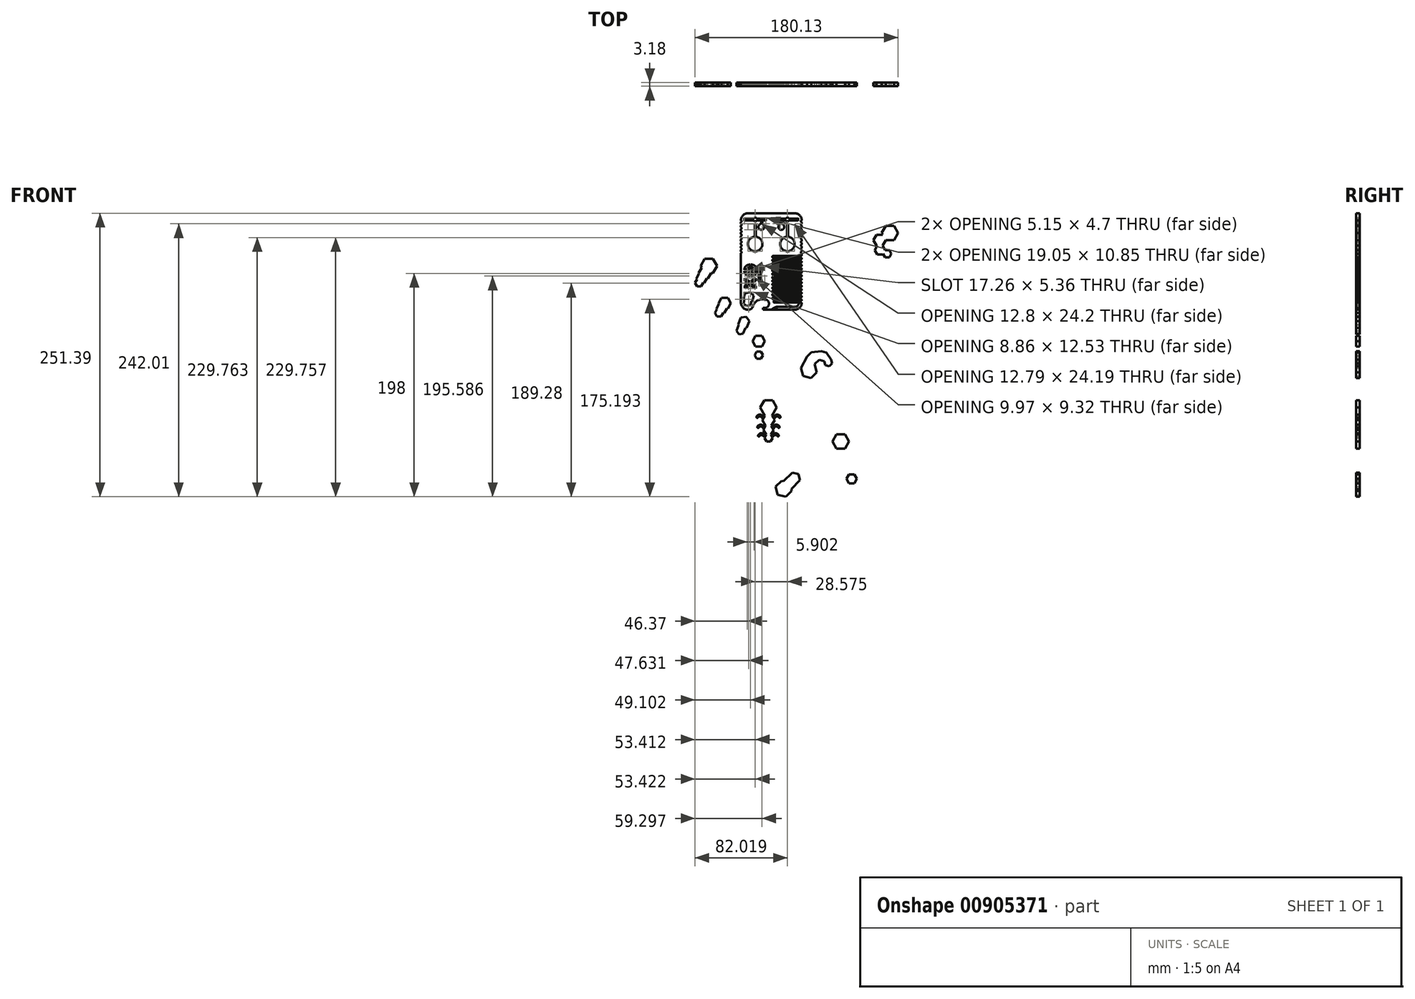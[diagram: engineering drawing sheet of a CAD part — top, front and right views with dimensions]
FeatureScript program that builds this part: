
annotation { "Feature Type Name" : "Feature", "Feature Type Description" : "" }
export const myFeature = defineFeature(function(context is Context, id is Id, definition is map)
    precondition{}
    {
        {
            var Q0;
            Q0=qCreatedBy(makeId("Front.planeOp"),FACE);
            var sketch = newSketch(context, id + "F0", { "sketchPlane" : qUnion([Q0])});
            skLineSegment(sketch, "E0.bottom", {"start": v(-20.64, 42.8) * mm, "end": v(20.64, 42.8) * mm});
            skLineSegment(sketch, "E0.top", {"start": v(-20.64, -42.8) * mm, "end": v(-20.41, -42.8) * mm});
            skLineSegment(sketch, "E0.left", {"start": v(-26.99, 34.92) * mm, "end": v(-26.99, 33.38) * mm});
            skLineSegment(sketch, "E0.right", {"start": v(26.99, 34.92) * mm, "end": v(26.99, 33.38) * mm});
            skPoint(sketch, "E1.visualSharp", {"position": v(-48.68, 30.1) * mm});
            skArc(sketch, "E1.filletArc", {"start": v(-20.64, 42.8) * mm, "mid": v(-25.13, 40.94) * mm, "end": v(-26.99, 36.45) * mm});
            skArc(sketch, "E2.filletArc", {"start": v(26.99, 36.45) * mm, "mid": v(25.13, 40.94) * mm, "end": v(20.64, 42.8) * mm});
            skPoint(sketch, "E3.visualSharp", {"position": v(26.99, -42.8) * mm});
            skArc(sketch, "E3.filletArc", {"start": v(20.64, -42.8) * mm, "mid": v(24.88, -41.17) * mm, "end": v(26.95, -37.12) * mm});
            skPoint(sketch, "E4.visualSharp", {"position": v(-26.99, -42.8) * mm});
            skArc(sketch, "E4.filletArc", {"start": v(-26.99, -36.45) * mm, "mid": v(-25.13, -40.94) * mm, "end": v(-20.64, -42.8) * mm});
            skLineSegment(sketch, "E5", {"start": v(-23.81, 36.45) * mm, "end": v(-23.81, 38.04) * mm});
            skLineSegment(sketch, "E6", {"start": v(-23.81, 38.04) * mm, "end": v(-15.89, 38.04) * mm});
            skLineSegment(sketch, "E7", {"start": v(-4.76, 38.04) * mm, "end": v(-4.76, 36.45) * mm});
            skLineSegment(sketch, "E8.MirrorCS", {"start": v(4.76, 38.04) * mm, "end": v(4.76, 36.45) * mm});
            skLineSegment(sketch, "E9.MirrorCS", {"start": v(23.81, 38.04) * mm, "end": v(15.89, 38.04) * mm});
            skLineSegment(sketch, "E10.MirrorCS", {"start": v(23.81, 36.45) * mm, "end": v(23.81, 38.04) * mm});
            skLineSegment(sketch, "E11", {"start": v(-26.99, -21.76) * mm, "end": v(-26.99, -13.82) * mm});
            skLineSegment(sketch, "E12", {"start": v(-26.99, -21.76) * mm, "end": v(-26.99, -26.81) * mm});
            skLineSegment(sketch, "E13", {"start": v(-26.99, -29.7) * mm, "end": v(-26.99, -21.76) * mm});
            skPoint(sketch, "E14.orphan", {"position": v(4.76, 36.45) * mm});
            skPoint(sketch, "E15.MirrorCS.end.orphan", {"position": v(23.81, 36.45) * mm});
            skLineSegment(sketch, "E16", {"start": v(4.76, 36.45) * mm, "end": v(8.29, 36.45) * mm});
            skPoint(sketch, "E17.center.orphan", {"position": v(0, -42.8) * mm});
            skLineSegment(sketch, "E18", {"start": v(-23.81, 36.45) * mm, "end": v(-15.68, 36.45) * mm});
            skLineSegment(sketch, "E19.trimOffspring", {"start": v(-7.21, -42.8) * mm, "end": v(20.64, -42.8) * mm});
            skLineSegment(sketch, "E20.MirrorCS", {"start": v(15.06, 25.6) * mm, "end": v(15.06, 25.6) * mm});
            skLineSegment(sketch, "E21.MirrorCS", {"start": v(13.53, 25.6) * mm, "end": v(13.53, 25.6) * mm});
            skLineSegment(sketch, "E22.MirrorCS", {"start": v(13.86, 33.27) * mm, "end": v(14.75, 33.27) * mm});
            skArc(sketch, "E23", {"start": v(-8.57, -4.37) * mm, "mid": v(-11.1, -13.04) * mm, "end": v(-8.32, -21.63) * mm});
            skLineSegment(sketch, "E24.MirrorCS", {"start": v(-13.53, 25.6) * mm, "end": v(-13.53, 25.6) * mm});
            skLineSegment(sketch, "E25.MirrorCS", {"start": v(-15.06, 25.6) * mm, "end": v(-15.06, 25.6) * mm});
            skLineSegment(sketch, "E26.MirrorCS", {"start": v(-13.86, 33.27) * mm, "end": v(-14.75, 33.27) * mm});
            skArc(sketch, "E27", {"start": v(-21.12, -9.85) * mm, "mid": v(-20, -10.35) * mm, "end": v(-18.78, -10.59) * mm});
            skArc(sketch, "E28", {"start": v(-16.8, -10.4) * mm, "mid": v(-15.43, -9.66) * mm, "end": v(-14.76, -8.24) * mm});
            skArc(sketch, "E29", {"start": v(-23.91, -8.25) * mm, "mid": v(-23.84, -8.95) * mm, "end": v(-23.69, -9.64) * mm});
            skArc(sketch, "E30", {"start": v(-23.69, -9.64) * mm, "mid": v(-23.34, -10.5) * mm, "end": v(-22.82, -11.27) * mm});
            skArc(sketch, "E31", {"start": v(-22.82, -11.27) * mm, "mid": v(-22.03, -12) * mm, "end": v(-21.08, -12.5) * mm});
            skArc(sketch, "E32", {"start": v(-21.08, -12.5) * mm, "mid": v(-19.95, -12.82) * mm, "end": v(-18.77, -12.94) * mm});
            skArc(sketch, "E33", {"start": v(-18.77, -12.94) * mm, "mid": v(-18.77, -12.94) * mm, "end": v(-18.77, -12.94) * mm});
            skArc(sketch, "E34", {"start": v(-17.14, -12.87) * mm, "mid": v(-16.37, -12.72) * mm, "end": v(-15.63, -12.48) * mm});
            skArc(sketch, "E35", {"start": v(-15.63, -12.48) * mm, "mid": v(-15.04, -12.2) * mm, "end": v(-14.5, -11.83) * mm});
            skArc(sketch, "E36", {"start": v(-14.5, -11.83) * mm, "mid": v(-13.97, -11.31) * mm, "end": v(-13.54, -10.71) * mm});
            skArc(sketch, "E37", {"start": v(-13.54, -10.71) * mm, "mid": v(-13.2, -10.02) * mm, "end": v(-13, -9.28) * mm});
            skArc(sketch, "E38", {"start": v(-13, -9.28) * mm, "mid": v(-12.91, -8.8) * mm, "end": v(-12.87, -8.32) * mm});
            skArc(sketch, "E39", {"start": v(-12.87, -8.32) * mm, "mid": v(-12.86, -8.28) * mm, "end": v(-12.86, -8.24) * mm});
            skLineSegment(sketch, "E40", {"start": v(-22.01, -7.86) * mm, "end": v(-22.02, -7.86) * mm});
            skLineSegment(sketch, "E41", {"start": v(-14.74, -7.83) * mm, "end": v(-14.73, -7.83) * mm});
            skLineSegment(sketch, "E42.trimOffspring", {"start": v(-21.98, -8.24) * mm, "end": v(-23.92, -8.25) * mm});
            skLineSegment(sketch, "E43", {"start": v(-13.81, -8.24) * mm, "end": v(-12.86, -8.24) * mm});
            skArc(sketch, "E44.trimOffspring", {"start": v(-12.85, -7.83) * mm, "mid": v(-12.85, -7.83) * mm, "end": v(-12.85, -7.82) * mm});
            skLineSegment(sketch, "E45.trimOffspring", {"start": v(-14.76, -8.24) * mm, "end": v(-13.81, -8.24) * mm});
            skArc(sketch, "E46.trimOffspring", {"start": v(-21.98, -8.24) * mm, "mid": v(-21.69, -9.12) * mm, "end": v(-21.12, -9.85) * mm});
            skPoint(sketch, "E47.orphan", {"position": v(-18.24, -10.6) * mm});
            skLineSegment(sketch, "E48", {"start": v(-22.02, -7.86) * mm, "end": v(-22.01, -7.86) * mm});
            skArc(sketch, "E49.MirrorCS", {"start": v(-21.98, -7.48) * mm, "mid": v(-21.7, -6.6) * mm, "end": v(-21.14, -5.86) * mm});
            skArc(sketch, "E50.MirrorCS", {"start": v(-21.14, -5.86) * mm, "mid": v(-20.02, -5.35) * mm, "end": v(-18.8, -5.1) * mm});
            skArc(sketch, "E51.MirrorCS", {"start": v(-16.83, -5.27) * mm, "mid": v(-15.44, -6) * mm, "end": v(-14.76, -7.4) * mm});
            skArc(sketch, "E52.MirrorCS", {"start": v(-12.87, -7.3) * mm, "mid": v(-12.87, -7.35) * mm, "end": v(-12.86, -7.4) * mm});
            skArc(sketch, "E53.MirrorCS", {"start": v(-13.01, -6.36) * mm, "mid": v(-12.92, -6.83) * mm, "end": v(-12.87, -7.3) * mm});
            skArc(sketch, "E54.MirrorCS", {"start": v(-13.56, -4.93) * mm, "mid": v(-13.23, -5.62) * mm, "end": v(-13.01, -6.36) * mm});
            skArc(sketch, "E55.MirrorCS", {"start": v(-14.54, -3.82) * mm, "mid": v(-14, -4.33) * mm, "end": v(-13.56, -4.93) * mm});
            skArc(sketch, "E56.MirrorCS", {"start": v(-15.67, -3.18) * mm, "mid": v(-15.08, -3.46) * mm, "end": v(-14.54, -3.82) * mm});
            skArc(sketch, "E57.MirrorCS", {"start": v(-17.19, -2.8) * mm, "mid": v(-16.42, -2.94) * mm, "end": v(-15.67, -3.18) * mm});
            skArc(sketch, "E58.MirrorCS", {"start": v(-18.82, -2.75) * mm, "mid": v(-18.82, -2.75) * mm, "end": v(-18.81, -2.75) * mm});
            skArc(sketch, "E59.MirrorCS", {"start": v(-21.13, -3.22) * mm, "mid": v(-20, -2.88) * mm, "end": v(-18.82, -2.75) * mm});
            skArc(sketch, "E60.MirrorCS", {"start": v(-22.85, -4.45) * mm, "mid": v(-22.07, -3.73) * mm, "end": v(-21.13, -3.22) * mm});
            skArc(sketch, "E61.MirrorCS", {"start": v(-23.7, -6.1) * mm, "mid": v(-23.37, -5.23) * mm, "end": v(-22.85, -4.45) * mm});
            skArc(sketch, "E62.MirrorCS", {"start": v(-23.92, -7.49) * mm, "mid": v(-23.85, -6.78) * mm, "end": v(-23.7, -6.1) * mm});
            skLineSegment(sketch, "E63.MirrorCS", {"start": v(-21.98, -7.48) * mm, "end": v(-23.92, -7.49) * mm});
            skLineSegment(sketch, "E64.MirrorCS", {"start": v(-14.76, -7.4) * mm, "end": v(-13.82, -7.4) * mm});
            skLineSegment(sketch, "E65.MirrorCS", {"start": v(-13.82, -7.4) * mm, "end": v(-12.86, -7.4) * mm});
            skArc(sketch, "E66", {"start": v(-14.73, -7.83) * mm, "mid": v(-14.73, -7.83) * mm, "end": v(-14.73, -7.82) * mm});
            skLineSegment(sketch, "E67.0", {"start": v(-18, -12.95) * mm, "end": v(-18.02, -10.6) * mm});
            skLineSegment(sketch, "E68.0", {"start": v(-18.77, -12.95) * mm, "end": v(-18.78, -10.59) * mm});
            skLineSegment(sketch, "E69.trimOffspring", {"start": v(-18.8, -5.1) * mm, "end": v(-18.81, -2.74) * mm});
            skPoint(sketch, "E70.orphan", {"position": v(-18.39, -7.84) * mm});
            skLineSegment(sketch, "E71.trimOffspring", {"start": v(-18.04, -5.08) * mm, "end": v(-18.05, -2.73) * mm});
            skPoint(sketch, "E72.MirrorCS.end.orphan", {"position": v(-14.73, -7.81) * mm});
            skPoint(sketch, "E72.MirrorCS.start.orphan", {"position": v(-14.76, -7.4) * mm});
            skPoint(sketch, "E73.MirrorCS.end.orphan", {"position": v(-12.85, -7.05) * mm});
            skPoint(sketch, "E73.MirrorCS.start.orphan", {"position": v(-12.86, -6.63) * mm});
            skPoint(sketch, "E74.orphan", {"position": v(-23.92, -7.87) * mm});
            skPoint(sketch, "E75.MirrorCS.end.orphan", {"position": v(-21.98, -7.48) * mm});
            skArc(sketch, "E76.trimOffspring", {"start": v(-18, -12.94) * mm, "mid": v(-17.57, -12.92) * mm, "end": v(-17.14, -12.87) * mm});
            skArc(sketch, "E77.trimOffspring", {"start": v(-18.02, -10.6) * mm, "mid": v(-17.4, -10.53) * mm, "end": v(-16.8, -10.4) * mm});
            skArc(sketch, "E78.trimOffspring", {"start": v(-18.04, -5.08) * mm, "mid": v(-17.43, -5.15) * mm, "end": v(-16.83, -5.27) * mm});
            skArc(sketch, "E79.trimOffspring", {"start": v(-18.05, -2.74) * mm, "mid": v(-17.62, -2.76) * mm, "end": v(-17.19, -2.8) * mm});
            skText(sketch, "E80", { "text": "X", "fontName": "OpenSans-Bold.ttf"});
            skArc(sketch, "E81", {"start": v(-7.21, -41) * mm, "mid": v(-2.22, -38.57) * mm, "end": v(-4.96, -33.74) * mm});
            skArc(sketch, "E82", {"start": v(-20.41, -42.8) * mm, "mid": v(-17.8, -41.93) * mm, "end": v(-16.25, -39.67) * mm});
            skArc(sketch, "E83", {"start": v(-4.96, -33.74) * mm, "mid": v(-10.34, -33.76) * mm, "end": v(-14.8, -36.76) * mm});
            skArc(sketch, "E84", {"start": v(-14.8, -36.76) * mm, "mid": v(-15.63, -38.17) * mm, "end": v(-16.25, -39.67) * mm});
            skLineSegment(sketch, "E85", {"start": v(-7.21, -41) * mm, "end": v(-7.21, -42.8) * mm});
            skLineSegment(sketch, "E86", {"start": v(-13.54, 21.83) * mm, "end": v(-13.53, 21.83) * mm});
            skLineSegment(sketch, "E87", {"start": v(26.99, 6.39) * mm, "end": v(26.99, 7.32) * mm});
            skLineSegment(sketch, "E88", {"start": v(2.84, -34.92) * mm, "end": v(26.23, -34.92) * mm});
            skArc(sketch, "E89", {"start": v(26.23, -34.92) * mm, "mid": v(26.99, -34.16) * mm, "end": v(26.23, -33.39) * mm});
            skLineSegment(sketch, "E90", {"start": v(26.23, -33.39) * mm, "end": v(1.59, -33.39) * mm});
            skArc(sketch, "E91", {"start": v(26.95, -37.12) * mm, "mid": v(26.72, -36.65) * mm, "end": v(26.22, -36.45) * mm});
            skPoint(sketch, "E92.start.orphan", {"position": v(26.99, -36.45) * mm});
            skArc(sketch, "E93", {"start": v(2.84, -34.92) * mm, "mid": v(2.09, -35.69) * mm, "end": v(2.84, -36.45) * mm});
            skLineSegment(sketch, "E94", {"start": v(2.84, -36.45) * mm, "end": v(26.22, -36.45) * mm});
            skArc(sketch, "E95", {"start": v(1.59, -31.86) * mm, "mid": v(0.83, -32.62) * mm, "end": v(1.59, -33.39) * mm});
            skLineSegment(sketch, "E96", {"start": v(1.59, -31.86) * mm, "end": v(26.23, -31.86) * mm});
            skArc(sketch, "E97", {"start": v(26.23, -31.86) * mm, "mid": v(26.99, -31.09) * mm, "end": v(26.23, -30.32) * mm});
            skLineSegment(sketch, "E98", {"start": v(26.23, -30.32) * mm, "end": v(1.59, -30.32) * mm});
            skLineSegment(sketch, "E99", {"start": v(1.59, -28.8) * mm, "end": v(26.23, -28.8) * mm});
            skArc(sketch, "E100", {"start": v(26.23, -28.8) * mm, "mid": v(26.99, -28.02) * mm, "end": v(26.23, -27.26) * mm});
            skLineSegment(sketch, "E101", {"start": v(26.23, -27.26) * mm, "end": v(1.59, -27.26) * mm});
            skArc(sketch, "E102", {"start": v(1.59, -25.72) * mm, "mid": v(0.83, -26.5) * mm, "end": v(1.59, -27.26) * mm});
            skLineSegment(sketch, "E103", {"start": v(1.59, -25.72) * mm, "end": v(26.23, -25.72) * mm});
            skArc(sketch, "E104", {"start": v(26.23, -25.72) * mm, "mid": v(26.99, -24.96) * mm, "end": v(26.23, -24.2) * mm});
            skLineSegment(sketch, "E105", {"start": v(26.23, -24.2) * mm, "end": v(1.59, -24.2) * mm});
            skLineSegment(sketch, "E106", {"start": v(1.59, -22.66) * mm, "end": v(26.23, -22.66) * mm});
            skArc(sketch, "E107", {"start": v(26.23, -22.66) * mm, "mid": v(26.99, -21.9) * mm, "end": v(26.23, -21.13) * mm});
            skLineSegment(sketch, "E108", {"start": v(26.23, -21.13) * mm, "end": v(1.59, -21.13) * mm});
            skArc(sketch, "E109", {"start": v(1.59, -22.66) * mm, "mid": v(0.83, -23.43) * mm, "end": v(1.59, -24.2) * mm});
            skArc(sketch, "E110", {"start": v(1.59, -19.6) * mm, "mid": v(0.83, -20.36) * mm, "end": v(1.59, -21.13) * mm});
            skLineSegment(sketch, "E111", {"start": v(1.59, -19.6) * mm, "end": v(26.23, -19.6) * mm});
            skArc(sketch, "E112", {"start": v(26.23, -19.6) * mm, "mid": v(26.99, -18.83) * mm, "end": v(26.23, -18.06) * mm});
            skLineSegment(sketch, "E113", {"start": v(26.23, -18.06) * mm, "end": v(1.59, -18.06) * mm});
            skArc(sketch, "E114", {"start": v(1.59, -16.53) * mm, "mid": v(0.83, -17.3) * mm, "end": v(1.59, -18.06) * mm});
            skLineSegment(sketch, "E115", {"start": v(1.59, -16.53) * mm, "end": v(26.23, -16.53) * mm});
            skArc(sketch, "E116", {"start": v(26.23, -16.53) * mm, "mid": v(26.99, -15.76) * mm, "end": v(26.23, -15) * mm});
            skLineSegment(sketch, "E117", {"start": v(26.23, -15) * mm, "end": v(1.59, -15) * mm});
            skArc(sketch, "E118", {"start": v(1.59, -13.46) * mm, "mid": v(0.83, -14.23) * mm, "end": v(1.59, -15) * mm});
            skLineSegment(sketch, "E119", {"start": v(1.59, -13.46) * mm, "end": v(26.23, -13.46) * mm});
            skArc(sketch, "E120", {"start": v(26.23, -13.46) * mm, "mid": v(26.99, -12.7) * mm, "end": v(26.23, -11.93) * mm});
            skLineSegment(sketch, "E121", {"start": v(26.23, -11.93) * mm, "end": v(1.59, -11.93) * mm});
            skArc(sketch, "E122", {"start": v(1.59, -10.4) * mm, "mid": v(0.83, -11.16) * mm, "end": v(1.59, -11.93) * mm});
            skLineSegment(sketch, "E123", {"start": v(1.59, -10.4) * mm, "end": v(26.23, -10.4) * mm});
            skArc(sketch, "E124", {"start": v(26.23, -10.4) * mm, "mid": v(26.99, -9.63) * mm, "end": v(26.23, -8.86) * mm});
            skLineSegment(sketch, "E125", {"start": v(26.23, -8.86) * mm, "end": v(1.59, -8.86) * mm});
            skArc(sketch, "E126", {"start": v(1.59, -7.33) * mm, "mid": v(0.83, -8.1) * mm, "end": v(1.59, -8.86) * mm});
            skLineSegment(sketch, "E127", {"start": v(1.59, -7.33) * mm, "end": v(26.23, -7.33) * mm});
            skArc(sketch, "E128", {"start": v(26.23, -7.33) * mm, "mid": v(26.99, -6.56) * mm, "end": v(26.23, -5.8) * mm});
            skLineSegment(sketch, "E129", {"start": v(26.23, -5.8) * mm, "end": v(1.59, -5.8) * mm});
            skArc(sketch, "E130", {"start": v(1.59, -4.26) * mm, "mid": v(0.83, -5.03) * mm, "end": v(1.59, -5.8) * mm});
            skLineSegment(sketch, "E131", {"start": v(1.59, -4.26) * mm, "end": v(26.23, -4.26) * mm});
            skArc(sketch, "E132", {"start": v(26.23, -4.26) * mm, "mid": v(26.99, -3.5) * mm, "end": v(26.23, -2.73) * mm});
            skLineSegment(sketch, "E133", {"start": v(26.23, -2.73) * mm, "end": v(1.59, -2.73) * mm});
            skArc(sketch, "E134", {"start": v(1.59, -1.2) * mm, "mid": v(0.83, -1.97) * mm, "end": v(1.59, -2.73) * mm});
            skLineSegment(sketch, "E135", {"start": v(1.59, -1.2) * mm, "end": v(26.23, -1.2) * mm});
            skArc(sketch, "E136", {"start": v(26.23, -1.2) * mm, "mid": v(26.99, -0.43) * mm, "end": v(26.23, 0.33) * mm});
            skLineSegment(sketch, "E137", {"start": v(26.23, 0.33) * mm, "end": v(1.59, 0.33) * mm});
            skArc(sketch, "E138", {"start": v(1.59, 1.87) * mm, "mid": v(0.83, 1.1) * mm, "end": v(1.59, 0.33) * mm});
            skLineSegment(sketch, "E139", {"start": v(1.59, 1.87) * mm, "end": v(26.23, 1.87) * mm});
            skArc(sketch, "E140", {"start": v(26.23, 1.87) * mm, "mid": v(26.99, 2.63) * mm, "end": v(26.23, 3.4) * mm});
            skLineSegment(sketch, "E141", {"start": v(26.23, 3.4) * mm, "end": v(1.59, 3.4) * mm});
            skArc(sketch, "E142", {"start": v(1.59, 4.93) * mm, "mid": v(0.83, 4.17) * mm, "end": v(1.59, 3.4) * mm});
            skLineSegment(sketch, "E143", {"start": v(1.59, 4.93) * mm, "end": v(26.23, 4.93) * mm});
            skArc(sketch, "E144", {"start": v(26.23, 4.93) * mm, "mid": v(26.77, 5.16) * mm, "end": v(26.99, 5.7) * mm});
            skLineSegment(sketch, "E145", {"start": v(26.99, 5.7) * mm, "end": v(26.99, 6.39) * mm});
            skLineSegment(sketch, "E146.0", {"start": v(-14.75, 33.27) * mm, "end": v(-14.75, 22.45) * mm});
            skLineSegment(sketch, "E147.0", {"start": v(-13.86, 33.27) * mm, "end": v(-13.86, 22.45) * mm});
            skLineSegment(sketch, "E148.0", {"start": v(13.86, 33.27) * mm, "end": v(13.86, 22.45) * mm});
            skLineSegment(sketch, "E149.0", {"start": v(14.75, 33.27) * mm, "end": v(14.75, 22.45) * mm});
            skArc(sketch, "E150", {"start": v(13.3, 21.82) * mm, "mid": v(14.33, 9.08) * mm, "end": v(15.27, 21.83) * mm});
            skArc(sketch, "E151", {"start": v(-15.3, 21.82) * mm, "mid": v(-14.28, 9.07) * mm, "end": v(-13.32, 21.83) * mm});
            skArc(sketch, "E152", {"start": v(-26.99, 7.32) * mm, "mid": v(-26.23, 8.1) * mm, "end": v(-26.99, 8.86) * mm});
            skArc(sketch, "E153", {"start": v(-26.99, 10.4) * mm, "mid": v(-26.23, 11.16) * mm, "end": v(-26.99, 11.92) * mm});
            skArc(sketch, "E154", {"start": v(-26.99, 13.46) * mm, "mid": v(-26.23, 14.22) * mm, "end": v(-26.99, 14.99) * mm});
            skArc(sketch, "E155", {"start": v(-26.99, 16.52) * mm, "mid": v(-26.23, 17.29) * mm, "end": v(-26.99, 18.05) * mm});
            skArc(sketch, "E156", {"start": v(-26.99, 19.59) * mm, "mid": v(-26.23, 20.35) * mm, "end": v(-26.99, 21.12) * mm});
            skArc(sketch, "E157", {"start": v(-26.99, 22.65) * mm, "mid": v(-26.23, 23.42) * mm, "end": v(-26.99, 24.19) * mm});
            skArc(sketch, "E158", {"start": v(-26.99, 25.72) * mm, "mid": v(-26.23, 26.49) * mm, "end": v(-26.99, 27.25) * mm});
            skArc(sketch, "E159", {"start": v(-26.99, 28.78) * mm, "mid": v(-26.23, 29.55) * mm, "end": v(-26.99, 30.32) * mm});
            skArc(sketch, "E160", {"start": v(-26.99, 31.85) * mm, "mid": v(-26.23, 32.62) * mm, "end": v(-26.99, 33.38) * mm});
            skArc(sketch, "E161", {"start": v(-26.99, 34.92) * mm, "mid": v(-26.23, 35.68) * mm, "end": v(-26.99, 36.45) * mm});
            skArc(sketch, "E162", {"start": v(26.99, 8.86) * mm, "mid": v(26.23, 8.1) * mm, "end": v(26.99, 7.32) * mm});
            skArc(sketch, "E163", {"start": v(26.99, 11.92) * mm, "mid": v(26.23, 11.16) * mm, "end": v(26.99, 10.4) * mm});
            skArc(sketch, "E164", {"start": v(26.99, 14.99) * mm, "mid": v(26.23, 14.22) * mm, "end": v(26.99, 13.46) * mm});
            skArc(sketch, "E165", {"start": v(26.99, 18.05) * mm, "mid": v(26.23, 17.29) * mm, "end": v(26.99, 16.52) * mm});
            skArc(sketch, "E166", {"start": v(26.99, 21.12) * mm, "mid": v(26.23, 20.35) * mm, "end": v(26.99, 19.59) * mm});
            skArc(sketch, "E167", {"start": v(26.99, 24.19) * mm, "mid": v(26.23, 23.42) * mm, "end": v(26.99, 22.65) * mm});
            skArc(sketch, "E168", {"start": v(26.99, 27.25) * mm, "mid": v(26.23, 26.49) * mm, "end": v(26.99, 25.72) * mm});
            skArc(sketch, "E169", {"start": v(26.99, 30.32) * mm, "mid": v(26.23, 29.55) * mm, "end": v(26.99, 28.78) * mm});
            skArc(sketch, "E170", {"start": v(26.99, 33.38) * mm, "mid": v(26.23, 32.62) * mm, "end": v(26.99, 31.85) * mm});
            skArc(sketch, "E171", {"start": v(26.99, 36.45) * mm, "mid": v(26.23, 35.68) * mm, "end": v(26.99, 34.92) * mm});
            skLineSegment(sketch, "E172.trimOffspring", {"start": v(-26.99, 7.32) * mm, "end": v(-26.99, -36.45) * mm});
            skLineSegment(sketch, "E173.trimOffspring", {"start": v(-26.99, 10.4) * mm, "end": v(-26.99, 8.86) * mm});
            skLineSegment(sketch, "E174.trimOffspring", {"start": v(-26.99, 13.46) * mm, "end": v(-26.99, 11.92) * mm});
            skLineSegment(sketch, "E175.trimOffspring", {"start": v(-26.99, 16.52) * mm, "end": v(-26.99, 14.99) * mm});
            skLineSegment(sketch, "E176.trimOffspring", {"start": v(-26.99, 19.59) * mm, "end": v(-26.99, 18.05) * mm});
            skLineSegment(sketch, "E177.trimOffspring", {"start": v(-26.99, 22.65) * mm, "end": v(-26.99, 21.12) * mm});
            skLineSegment(sketch, "E178.trimOffspring", {"start": v(-26.99, 25.72) * mm, "end": v(-26.99, 24.19) * mm});
            skLineSegment(sketch, "E179.trimOffspring", {"start": v(-26.99, 28.78) * mm, "end": v(-26.99, 27.25) * mm});
            skLineSegment(sketch, "E180.trimOffspring", {"start": v(-26.99, 31.85) * mm, "end": v(-26.99, 30.32) * mm});
            skLineSegment(sketch, "E181.trimOffspring", {"start": v(26.99, 31.85) * mm, "end": v(26.99, 30.32) * mm});
            skLineSegment(sketch, "E182.trimOffspring", {"start": v(26.99, 28.78) * mm, "end": v(26.99, 27.25) * mm});
            skLineSegment(sketch, "E183.trimOffspring", {"start": v(26.99, 25.72) * mm, "end": v(26.99, 24.19) * mm});
            skLineSegment(sketch, "E184.trimOffspring", {"start": v(26.99, 22.65) * mm, "end": v(26.99, 21.12) * mm});
            skLineSegment(sketch, "E185.trimOffspring", {"start": v(26.99, 19.59) * mm, "end": v(26.99, 18.05) * mm});
            skLineSegment(sketch, "E186.trimOffspring", {"start": v(26.99, 16.52) * mm, "end": v(26.99, 14.99) * mm});
            skLineSegment(sketch, "E187.trimOffspring", {"start": v(26.99, 13.46) * mm, "end": v(26.99, 11.92) * mm});
            skLineSegment(sketch, "E188.trimOffspring", {"start": v(26.99, 10.4) * mm, "end": v(26.99, 8.86) * mm});
            skLineSegment(sketch, "E189", {"start": v(-6.04, -4.37) * mm, "end": v(-8.57, -4.37) * mm});
            skLineSegment(sketch, "E190", {"start": v(-8.57, -4.37) * mm, "end": v(-6.04, -4.37) * mm});
            skCircle(sketch, "E191", {"center": v(-18.39, -7.84) * mm, "radius": 1.3 * mm});
            skPoint(sketch, "E192.orphan", {"position": v(-14.3, 33.27) * mm});
            skLineSegment(sketch, "E193.trimOffspring", {"start": v(-12.71, 38.04) * mm, "end": v(-4.76, 38.04) * mm});
            skPoint(sketch, "E194.endSnap0", {"position": v(14.29, 38.04) * mm});
            skLineSegment(sketch, "E195.trimOffspring", {"start": v(12.71, 38.04) * mm, "end": v(4.76, 38.04) * mm});
            skLineSegment(sketch, "E196.trimOffspring", {"start": v(14.3, 38.04) * mm, "end": v(14.29, 38.04) * mm});
            skPoint(sketch, "E194.start.orphan", {"position": v(14.3, 33.27) * mm});
            skLineSegment(sketch, "E197", {"start": v(12.71, 38.04) * mm, "end": v(12.9, 38.04) * mm});
            skArc(sketch, "E198", {"start": v(15.68, 38.04) * mm, "mid": v(14.29, 38.84) * mm, "end": v(12.9, 38.04) * mm});
            skLineSegment(sketch, "E199.trimOffspring", {"start": v(14.29, 38.04) * mm, "end": v(14.3, 38.04) * mm});
            skLineSegment(sketch, "E200.trimOffspring", {"start": v(15.68, 38.04) * mm, "end": v(15.89, 38.04) * mm});
            skPoint(sketch, "E201.end.orphan", {"position": v(14.3, 36.45) * mm});
            skLineSegment(sketch, "E202.trimOffspring", {"start": v(15.68, 36.45) * mm, "end": v(23.81, 36.45) * mm});
            skArc(sketch, "E203.trimOffspring", {"start": v(12.9, 36.45) * mm, "mid": v(14.29, 35.64) * mm, "end": v(15.68, 36.45) * mm});
            skLineSegment(sketch, "E204", {"start": v(-15.89, 38.04) * mm, "end": v(-15.68, 38.04) * mm});
            skPoint(sketch, "E205.orphan", {"position": v(8.83, 36.45) * mm});
            skPoint(sketch, "E206.start.orphan", {"position": v(8.83, 33.27) * mm});
            skLineSegment(sketch, "E207.trimOffspring", {"start": v(9.28, 36.45) * mm, "end": v(12.9, 36.45) * mm});
            skArc(sketch, "E208.MirrorCS", {"start": v(-15.68, 38.04) * mm, "mid": v(-14.29, 38.84) * mm, "end": v(-12.9, 38.04) * mm});
            skArc(sketch, "E209.MirrorCS", {"start": v(-12.9, 36.45) * mm, "mid": v(-14.29, 35.64) * mm, "end": v(-15.68, 36.45) * mm});
            skPoint(sketch, "E210.start.orphan", {"position": v(0, 42.8) * mm});
            skLineSegment(sketch, "E211.trimOffspring", {"start": v(-12.9, 36.45) * mm, "end": v(-9.28, 36.45) * mm});
            skLineSegment(sketch, "E212.trimOffspring", {"start": v(-12.9, 38.04) * mm, "end": v(-12.71, 38.04) * mm});
            skLineSegment(sketch, "E213.trimOffspring", {"start": v(-8.29, 36.45) * mm, "end": v(-4.76, 36.45) * mm});
            skArc(sketch, "E214", {"start": v(-9.9, 33.04) * mm, "mid": v(-8.95, 34.63) * mm, "end": v(-9.28, 36.45) * mm});
            skArc(sketch, "E215.0", {"start": v(-8.4, 33.52) * mm, "mid": v(-8.02, 34.97) * mm, "end": v(-8.29, 36.45) * mm});
            skArc(sketch, "E216.MirrorCS", {"start": v(8.4, 33.52) * mm, "mid": v(8.02, 34.97) * mm, "end": v(8.29, 36.45) * mm});
            skArc(sketch, "E217.MirrorCS", {"start": v(9.9, 33.04) * mm, "mid": v(8.95, 34.63) * mm, "end": v(9.28, 36.45) * mm});
            skArc(sketch, "E218.MirrorCS", {"start": v(9.9, 33.04) * mm, "mid": v(8.58, 28) * mm, "end": v(8.25, 33.2) * mm});
            skPoint(sketch, "E219.orphan", {"position": v(9.94, 33.02) * mm});
            skPoint(sketch, "E220.start.orphan", {"position": v(-9.9, 33.04) * mm});
            skArc(sketch, "E221.MirrorCS", {"start": v(-9.9, 33.04) * mm, "mid": v(-8.58, 28) * mm, "end": v(-8.25, 33.2) * mm});
            skPoint(sketch, "E222.orphan", {"position": v(-9.94, 33.02) * mm});
            skArc(sketch, "E223.0", {"start": v(-6.04, -4.37) * mm, "mid": v(-9.04, -13.06) * mm, "end": v(-5.74, -21.63) * mm});
            skLineSegment(sketch, "E224", {"start": v(-8.32, -21.63) * mm, "end": v(-5.74, -21.63) * mm});
            skArc(sketch, "E225", {"start": v(-15.3, 21.82) * mm, "mid": v(-14.92, 22.04) * mm, "end": v(-14.75, 22.45) * mm});
            skArc(sketch, "E226.MirrorCS", {"start": v(-13.3, 21.82) * mm, "mid": v(-13.69, 22.04) * mm, "end": v(-13.86, 22.45) * mm});
            skArc(sketch, "E227.MirrorCS", {"start": v(15.3, 21.82) * mm, "mid": v(14.92, 22.04) * mm, "end": v(14.75, 22.45) * mm});
            skArc(sketch, "E228.MirrorCS", {"start": v(13.3, 21.82) * mm, "mid": v(13.69, 22.04) * mm, "end": v(13.86, 22.45) * mm});
            skArc(sketch, "E229", {"start": v(-8.4, 33.52) * mm, "mid": v(-8.4, 33.33) * mm, "end": v(-8.25, 33.2) * mm});
            skArc(sketch, "E230.MirrorCS", {"start": v(8.4, 33.52) * mm, "mid": v(8.4, 33.33) * mm, "end": v(8.25, 33.2) * mm});
            skLineSegment(sketch, "E231.2", {"start": v(-22.9, -58.86) * mm, "end": v(-25.03, -64.01) * mm});
            skLineSegment(sketch, "E231.3", {"start": v(-25.03, -64.01) * mm, "end": v(-28.7, -64.5) * mm});
            skLineSegment(sketch, "E231.4", {"start": v(-28.7, -64.5) * mm, "end": v(-30.97, -61.56) * mm});
            skLineSegment(sketch, "E231.5", {"start": v(-30.97, -61.56) * mm, "end": v(-28.84, -56.4) * mm});
            skLineSegment(sketch, "E232.0", {"start": v(-26.92, -49.76) * mm, "end": v(-22.37, -49.16) * mm});
            skLineSegment(sketch, "E232.1", {"start": v(-22.37, -49.16) * mm, "end": v(-19.58, -52.8) * mm});
            skLineSegment(sketch, "E232.2", {"start": v(-19.58, -52.8) * mm, "end": v(-22.03, -58.74) * mm});
            skLineSegment(sketch, "E232.5", {"start": v(-29.38, -55.71) * mm, "end": v(-26.92, -49.76) * mm});
            skArc(sketch, "E233", {"start": v(1.59, -28.8) * mm, "mid": v(0.83, -29.56) * mm, "end": v(1.59, -30.32) * mm});
            skLineSegment(sketch, "E234", {"start": v(-28.83, -56.42) * mm, "end": v(-28.84, -56.41) * mm});
            skLineSegment(sketch, "E235", {"start": v(-28.84, -56.41) * mm, "end": v(-28.83, -56.42) * mm});
            skLineSegment(sketch, "E236.0", {"start": v(-28.83, -56.42) * mm, "end": v(-29.38, -55.71) * mm});
            skLineSegment(sketch, "E237.0", {"start": v(-22.03, -58.74) * mm, "end": v(-22.9, -58.86) * mm});
            skCircle(sketch, "E238.cCircle", {"center": v(-11.11, -82.91) * mm, "radius": 3.17 * mm, "construction": true});
            skLineSegment(sketch, "E238.0", {"start": v(-12.94, -79.74) * mm, "end": v(-9.28, -79.74) * mm});
            skLineSegment(sketch, "E238.1", {"start": v(-9.28, -79.74) * mm, "end": v(-7.44, -82.91) * mm});
            skLineSegment(sketch, "E238.2", {"start": v(-7.44, -82.91) * mm, "end": v(-9.28, -86.09) * mm});
            skLineSegment(sketch, "E238.3", {"start": v(-9.28, -86.09) * mm, "end": v(-12.94, -86.09) * mm});
            skLineSegment(sketch, "E238.4", {"start": v(-12.94, -86.09) * mm, "end": v(-14.78, -82.91) * mm});
            skLineSegment(sketch, "E238.5", {"start": v(-14.78, -82.91) * mm, "end": v(-12.94, -79.74) * mm});
            skPoint(sketch, "E238.0.midPoint", {"position": v(-11.11, -79.74) * mm});
            skLineSegment(sketch, "E239.0", {"start": v(-23.4, -28.51) * mm, "end": v(-19.03, -27.13) * mm});
            skLineSegment(sketch, "E239.1", {"start": v(-19.03, -27.13) * mm, "end": v(-15.65, -30.23) * mm});
            skLineSegment(sketch, "E239.2", {"start": v(-15.65, -30.23) * mm, "end": v(-16.64, -34.7) * mm});
            skLineSegment(sketch, "E239.3", {"start": v(-16.64, -34.7) * mm, "end": v(-17.52, -34.98) * mm});
            skLineSegment(sketch, "E239.4", {"start": v(-23.72, -33.6) * mm, "end": v(-24.4, -32.98) * mm});
            skLineSegment(sketch, "E239.5", {"start": v(-24.4, -32.98) * mm, "end": v(-23.4, -28.51) * mm});
            skCircle(sketch, "E240.cCircle", {"center": v(-11.2, -70.52) * mm, "radius": 4.76 * mm, "construction": true});
            skLineSegment(sketch, "E240.0", {"start": v(-13.94, -65.76) * mm, "end": v(-8.44, -65.76) * mm});
            skLineSegment(sketch, "E240.1", {"start": v(-8.44, -65.76) * mm, "end": v(-5.7, -70.52) * mm});
            skLineSegment(sketch, "E240.2", {"start": v(-5.7, -70.52) * mm, "end": v(-8.44, -75.28) * mm});
            skLineSegment(sketch, "E240.3", {"start": v(-8.44, -75.28) * mm, "end": v(-13.94, -75.28) * mm});
            skLineSegment(sketch, "E240.4", {"start": v(-13.94, -75.28) * mm, "end": v(-16.7, -70.52) * mm});
            skLineSegment(sketch, "E240.5", {"start": v(-16.7, -70.52) * mm, "end": v(-13.94, -65.76) * mm});
            skPoint(sketch, "E240.0.midPoint", {"position": v(-11.2, -65.76) * mm});
            skLineSegment(sketch, "E241.0", {"start": v(-59, 2.49) * mm, "end": v(-51.67, 2.49) * mm});
            skLineSegment(sketch, "E241.1", {"start": v(-51.67, 2.49) * mm, "end": v(-48, -3.86) * mm});
            skLineSegment(sketch, "E241.2", {"start": v(-48, -3.86) * mm, "end": v(-51.67, -10.21) * mm});
            skLineSegment(sketch, "E241.3", {"start": v(-51.67, -10.21) * mm, "end": v(-53.5, -10.21) * mm});
            skLineSegment(sketch, "E241.4", {"start": v(-61.75, -5.45) * mm, "end": v(-62.67, -3.86) * mm});
            skLineSegment(sketch, "E241.5", {"start": v(-62.67, -3.86) * mm, "end": v(-59, 2.49) * mm});
            skPoint(sketch, "E241.0.midPoint", {"position": v(-55.34, 2.49) * mm});
            skCircle(sketch, "E242.cCircle", {"center": v(50.33, -89.34) * mm, "radius": 3.17 * mm, "construction": true});
            skLineSegment(sketch, "E242.0", {"start": v(46.79, -88.39) * mm, "end": v(49.38, -85.8) * mm});
            skLineSegment(sketch, "E242.1", {"start": v(49.38, -85.8) * mm, "end": v(52.92, -86.74) * mm});
            skLineSegment(sketch, "E242.2", {"start": v(52.92, -86.74) * mm, "end": v(53.87, -90.28) * mm});
            skLineSegment(sketch, "E242.3", {"start": v(53.87, -90.28) * mm, "end": v(51.28, -92.88) * mm});
            skLineSegment(sketch, "E242.4", {"start": v(51.28, -92.88) * mm, "end": v(47.74, -91.93) * mm});
            skLineSegment(sketch, "E242.5", {"start": v(47.74, -91.93) * mm, "end": v(46.79, -88.39) * mm});
            skPoint(sketch, "E242.0.midPoint", {"position": v(48.08, -87.1) * mm});
            skCircle(sketch, "E243.cCircle", {"center": v(45.6, -83.96) * mm, "radius": 3.97 * mm, "construction": true});
            skLineSegment(sketch, "E243.0", {"start": v(41.17, -82.77) * mm, "end": v(44.41, -79.53) * mm});
            skLineSegment(sketch, "E243.1", {"start": v(44.41, -79.53) * mm, "end": v(48.84, -80.72) * mm});
            skLineSegment(sketch, "E243.2", {"start": v(48.84, -80.72) * mm, "end": v(50.03, -85.15) * mm});
            skLineSegment(sketch, "E243.3", {"start": v(50.03, -85.15) * mm, "end": v(46.79, -88.39) * mm});
            skLineSegment(sketch, "E243.4", {"start": v(46.79, -88.39) * mm, "end": v(42.36, -87.2) * mm});
            skLineSegment(sketch, "E243.5", {"start": v(42.36, -87.2) * mm, "end": v(41.17, -82.77) * mm});
            skPoint(sketch, "E243.0.midPoint", {"position": v(42.8, -81.15) * mm});
            skCircle(sketch, "E244.cCircle", {"center": v(37.05, -85.78) * mm, "radius": 4.76 * mm, "construction": true});
            skLineSegment(sketch, "E244.0", {"start": v(31.74, -84.35) * mm, "end": v(35.62, -80.47) * mm});
            skLineSegment(sketch, "E244.1", {"start": v(35.62, -80.47) * mm, "end": v(40.94, -81.89) * mm});
            skLineSegment(sketch, "E244.2", {"start": v(40.94, -81.89) * mm, "end": v(42.36, -87.2) * mm});
            skLineSegment(sketch, "E244.3", {"start": v(42.36, -87.2) * mm, "end": v(38.47, -91.09) * mm});
            skLineSegment(sketch, "E244.4", {"start": v(38.47, -91.09) * mm, "end": v(33.16, -89.67) * mm});
            skLineSegment(sketch, "E244.5", {"start": v(33.16, -89.67) * mm, "end": v(31.74, -84.35) * mm});
            skPoint(sketch, "E244.0.midPoint", {"position": v(33.68, -82.4) * mm});
            skCircle(sketch, "E245.cCircle", {"center": v(33.29, -96.27) * mm, "radius": 6.35 * mm, "construction": true});
            skLineSegment(sketch, "E245.0", {"start": v(26.2, -94.38) * mm, "end": v(31.39, -89.2) * mm});
            skLineSegment(sketch, "E245.1", {"start": v(31.39, -89.2) * mm, "end": v(38.47, -91.09) * mm});
            skLineSegment(sketch, "E245.2", {"start": v(38.47, -91.09) * mm, "end": v(40.37, -98.17) * mm});
            skLineSegment(sketch, "E245.4", {"start": v(35.18, -103.36) * mm, "end": v(28.1, -101.46) * mm});
            skLineSegment(sketch, "E245.5", {"start": v(28.1, -101.46) * mm, "end": v(26.2, -94.38) * mm});
            skPoint(sketch, "E245.0.midPoint", {"position": v(28.8, -91.78) * mm});
            skLineSegment(sketch, "E246", {"start": v(35.18, -103.36) * mm, "end": v(40.37, -98.17) * mm});
            skLineSegment(sketch, "E247", {"start": v(26.2, -94.38) * mm, "end": v(31.74, -84.35) * mm});
            skLineSegment(sketch, "E248", {"start": v(35.62, -80.47) * mm, "end": v(44.41, -79.53) * mm});
            skLineSegment(sketch, "E249", {"start": v(48.84, -80.72) * mm, "end": v(52.92, -86.74) * mm});
            skLineSegment(sketch, "E250.0", {"start": v(10.86, -194.9) * mm, "end": v(18.64, -187.12) * mm});
            skLineSegment(sketch, "E250.1", {"start": v(18.64, -187.12) * mm, "end": v(23.95, -188.54) * mm});
            skLineSegment(sketch, "E250.2", {"start": v(23.95, -188.54) * mm, "end": v(25.37, -193.85) * mm});
            skLineSegment(sketch, "E250.3", {"start": v(25.37, -193.85) * mm, "end": v(17.6, -201.63) * mm});
            skLineSegment(sketch, "E251.0", {"start": v(3.9, -199.6) * mm, "end": v(9.1, -194.42) * mm});
            skLineSegment(sketch, "E251.1", {"start": v(9.1, -194.42) * mm, "end": v(10.86, -194.9) * mm});
            skLineSegment(sketch, "E251.2", {"start": v(17.6, -201.63) * mm, "end": v(18.07, -203.4) * mm});
            skLineSegment(sketch, "E251.3", {"start": v(18.07, -203.4) * mm, "end": v(12.89, -208.59) * mm});
            skLineSegment(sketch, "E251.4", {"start": v(12.89, -208.59) * mm, "end": v(5.8, -206.69) * mm});
            skLineSegment(sketch, "E251.5", {"start": v(5.8, -206.69) * mm, "end": v(3.9, -199.6) * mm});
            skLineSegment(sketch, "E252.2", {"start": v(-17.52, -34.98) * mm, "end": v(-18.3, -38.56) * mm});
            skLineSegment(sketch, "E252.3", {"start": v(-18.3, -38.56) * mm, "end": v(-21.8, -39.66) * mm});
            skLineSegment(sketch, "E252.4", {"start": v(-21.8, -39.66) * mm, "end": v(-24.5, -37.18) * mm});
            skLineSegment(sketch, "E252.5", {"start": v(-24.5, -37.18) * mm, "end": v(-23.72, -33.6) * mm});
            skCircle(sketch, "E253.cCircle", {"center": v(71.21, -192.68) * mm, "radius": 3.97 * mm, "construction": true});
            skLineSegment(sketch, "E253.0", {"start": v(68.92, -188.7) * mm, "end": v(73.5, -188.7) * mm});
            skLineSegment(sketch, "E253.1", {"start": v(73.5, -188.7) * mm, "end": v(75.8, -192.68) * mm});
            skLineSegment(sketch, "E253.2", {"start": v(75.8, -192.68) * mm, "end": v(73.5, -196.65) * mm});
            skLineSegment(sketch, "E253.3", {"start": v(73.5, -196.65) * mm, "end": v(68.92, -196.65) * mm});
            skLineSegment(sketch, "E253.4", {"start": v(68.92, -196.65) * mm, "end": v(66.63, -192.68) * mm});
            skLineSegment(sketch, "E253.5", {"start": v(66.63, -192.68) * mm, "end": v(68.92, -188.7) * mm});
            skPoint(sketch, "E253.0.midPoint", {"position": v(71.21, -188.7) * mm});
            skLineSegment(sketch, "E254.0", {"start": v(-44.05, -32.18) * mm, "end": v(-38.55, -32.18) * mm});
            skLineSegment(sketch, "E254.1", {"start": v(-38.55, -32.18) * mm, "end": v(-35.8, -36.94) * mm});
            skLineSegment(sketch, "E254.2", {"start": v(-35.8, -36.94) * mm, "end": v(-38.55, -41.7) * mm});
            skLineSegment(sketch, "E254.3", {"start": v(-38.55, -41.7) * mm, "end": v(-39.47, -41.7) * mm});
            skLineSegment(sketch, "E254.4", {"start": v(-46.34, -37.73) * mm, "end": v(-46.8, -36.94) * mm});
            skLineSegment(sketch, "E254.5", {"start": v(-46.8, -36.94) * mm, "end": v(-44.05, -32.18) * mm});
            skCircle(sketch, "E255.cCircle", {"center": v(61.54, -159.46) * mm, "radius": 6.35 * mm, "construction": true});
            skLineSegment(sketch, "E255.0", {"start": v(57.88, -153.11) * mm, "end": v(65.2, -153.11) * mm});
            skLineSegment(sketch, "E255.1", {"start": v(65.2, -153.11) * mm, "end": v(68.87, -159.46) * mm});
            skLineSegment(sketch, "E255.2", {"start": v(68.87, -159.46) * mm, "end": v(65.2, -165.81) * mm});
            skLineSegment(sketch, "E255.3", {"start": v(65.2, -165.81) * mm, "end": v(57.88, -165.81) * mm});
            skLineSegment(sketch, "E255.4", {"start": v(57.88, -165.81) * mm, "end": v(54.2, -159.46) * mm});
            skLineSegment(sketch, "E255.5", {"start": v(54.2, -159.46) * mm, "end": v(57.88, -153.11) * mm});
            skPoint(sketch, "E255.0.midPoint", {"position": v(61.54, -153.11) * mm});
            skLineSegment(sketch, "E256.0", {"start": v(33.29, -96.27) * mm, "end": v(28.8, -91.78) * mm, "construction": true});
            skLineSegment(sketch, "E257.0", {"start": v(37.05, -85.78) * mm, "end": v(33.68, -82.4) * mm, "construction": true});
            skLineSegment(sketch, "E258.0", {"start": v(50.33, -89.34) * mm, "end": v(48.08, -87.1) * mm, "construction": true});
            skLineSegment(sketch, "E259.0", {"start": v(45.6, -83.96) * mm, "end": v(42.8, -81.15) * mm, "construction": true});
            skLineSegment(sketch, "E260.2", {"start": v(1.16, -156.37) * mm, "end": v(-0.67, -159.54) * mm});
            skLineSegment(sketch, "E260.3", {"start": v(-0.67, -159.54) * mm, "end": v(-4.34, -159.54) * mm});
            skLineSegment(sketch, "E260.4", {"start": v(-4.34, -159.54) * mm, "end": v(-6.17, -156.37) * mm});
            skLineSegment(sketch, "E260.5", {"start": v(-6.17, -156.37) * mm, "end": v(-4.57, -153.59) * mm});
            skLineSegment(sketch, "E261.1", {"start": v(0.02, -145.65) * mm, "end": v(2.08, -149.22) * mm});
            skLineSegment(sketch, "E261.2", {"start": v(2.08, -149.22) * mm, "end": v(-0.44, -153.59) * mm});
            skLineSegment(sketch, "E261.4", {"start": v(-4.57, -153.59) * mm, "end": v(-7.09, -149.22) * mm});
            skLineSegment(sketch, "E261.5", {"start": v(-7.09, -149.22) * mm, "end": v(-5.02, -145.65) * mm});
            skLineSegment(sketch, "E262.1", {"start": v(0.7, -136.52) * mm, "end": v(3, -140.5) * mm});
            skLineSegment(sketch, "E262.2", {"start": v(3, -140.5) * mm, "end": v(0.02, -145.65) * mm});
            skLineSegment(sketch, "E262.4", {"start": v(-5.02, -145.65) * mm, "end": v(-8, -140.5) * mm});
            skLineSegment(sketch, "E262.5", {"start": v(-8, -140.5) * mm, "end": v(-5.71, -136.52) * mm});
            skLineSegment(sketch, "E263.0", {"start": v(-6.17, -123.03) * mm, "end": v(1.16, -123.03) * mm});
            skLineSegment(sketch, "E263.1", {"start": v(1.16, -123.03) * mm, "end": v(4.83, -129.38) * mm});
            skLineSegment(sketch, "E263.2", {"start": v(4.83, -129.38) * mm, "end": v(0.7, -136.52) * mm});
            skLineSegment(sketch, "E263.4", {"start": v(-5.71, -136.52) * mm, "end": v(-9.84, -129.38) * mm});
            skLineSegment(sketch, "E263.5", {"start": v(-9.84, -129.38) * mm, "end": v(-6.17, -123.03) * mm});
            skPoint(sketch, "E264.startSnap0", {"position": v(2.95, -137.87) * mm});
            skArc(sketch, "E265.0", {"start": v(8.13, -137.54) * mm, "mid": v(5.2, -135.7) * mm, "end": v(2.26, -137.54) * mm});
            skArc(sketch, "E266.0", {"start": v(6.75, -138.2) * mm, "mid": v(5.2, -137.22) * mm, "end": v(3.64, -138.2) * mm});
            skArc(sketch, "E267", {"start": v(2.26, -137.54) * mm, "mid": v(2.62, -138.56) * mm, "end": v(3.64, -138.2) * mm});
            skArc(sketch, "E268", {"start": v(6.75, -138.2) * mm, "mid": v(7.77, -138.56) * mm, "end": v(8.13, -137.54) * mm});
            skPoint(sketch, "E269.startSnap0", {"position": v(2.15, -146.8) * mm});
            skArc(sketch, "E270.0", {"start": v(7.33, -146.47) * mm, "mid": v(4.4, -144.62) * mm, "end": v(1.46, -146.47) * mm});
            skArc(sketch, "E271.0", {"start": v(5.95, -147.13) * mm, "mid": v(4.4, -146.15) * mm, "end": v(2.84, -147.13) * mm});
            skArc(sketch, "E272", {"start": v(1.46, -146.47) * mm, "mid": v(1.82, -147.49) * mm, "end": v(2.84, -147.13) * mm});
            skArc(sketch, "E273", {"start": v(5.95, -147.13) * mm, "mid": v(6.97, -147.49) * mm, "end": v(7.33, -146.47) * mm});
            skLineSegment(sketch, "E274.1", {"start": v(-0.44, -153.59) * mm, "end": v(1.16, -156.37) * mm});
            skPoint(sketch, "E275.startSnap0", {"position": v(1.46, -154.34) * mm});
            skArc(sketch, "E276.0", {"start": v(6.64, -154.01) * mm, "mid": v(3.7, -152.17) * mm, "end": v(0.77, -154.01) * mm});
            skArc(sketch, "E277.0", {"start": v(5.26, -154.67) * mm, "mid": v(3.7, -153.69) * mm, "end": v(2.15, -154.67) * mm});
            skArc(sketch, "E278", {"start": v(0.77, -154.01) * mm, "mid": v(1.13, -155.03) * mm, "end": v(2.15, -154.67) * mm});
            skArc(sketch, "E279", {"start": v(5.26, -154.67) * mm, "mid": v(6.28, -155.03) * mm, "end": v(6.64, -154.01) * mm});
            skArc(sketch, "E280.MirrorCS", {"start": v(-5.78, -154.01) * mm, "mid": v(-6.14, -155.03) * mm, "end": v(-7.15, -154.67) * mm});
            skArc(sketch, "E281.MirrorCS", {"start": v(-11.64, -154.01) * mm, "mid": v(-8.71, -152.17) * mm, "end": v(-5.78, -154.01) * mm});
            skArc(sketch, "E282.MirrorCS", {"start": v(-10.27, -154.67) * mm, "mid": v(-8.71, -153.69) * mm, "end": v(-7.15, -154.67) * mm});
            skArc(sketch, "E283.MirrorCS", {"start": v(-10.27, -154.67) * mm, "mid": v(-11.29, -155.03) * mm, "end": v(-11.64, -154.01) * mm});
            skArc(sketch, "E284.MirrorCS", {"start": v(-10.96, -147.13) * mm, "mid": v(-9.4, -146.15) * mm, "end": v(-7.84, -147.13) * mm});
            skArc(sketch, "E285.MirrorCS", {"start": v(-6.47, -146.47) * mm, "mid": v(-6.83, -147.49) * mm, "end": v(-7.84, -147.13) * mm});
            skArc(sketch, "E286.MirrorCS", {"start": v(-12.33, -146.47) * mm, "mid": v(-9.4, -144.62) * mm, "end": v(-6.47, -146.47) * mm});
            skArc(sketch, "E287.MirrorCS", {"start": v(-10.96, -147.13) * mm, "mid": v(-11.97, -147.49) * mm, "end": v(-12.33, -146.47) * mm});
            skArc(sketch, "E288.MirrorCS", {"start": v(-13.13, -137.54) * mm, "mid": v(-10.2, -135.7) * mm, "end": v(-7.27, -137.54) * mm});
            skArc(sketch, "E289.MirrorCS", {"start": v(-11.76, -138.2) * mm, "mid": v(-10.2, -137.22) * mm, "end": v(-8.64, -138.2) * mm});
            skArc(sketch, "E290.MirrorCS", {"start": v(-7.27, -137.54) * mm, "mid": v(-7.63, -138.56) * mm, "end": v(-8.64, -138.2) * mm});
            skArc(sketch, "E291.MirrorCS", {"start": v(-11.76, -138.2) * mm, "mid": v(-12.78, -138.56) * mm, "end": v(-13.13, -137.54) * mm});
            skCircle(sketch, "E292.cCircle", {"center": v(105.09, 25.13) * mm, "radius": 6.35 * mm, "construction": true});
            skLineSegment(sketch, "E292.0", {"start": v(101.42, 31.48) * mm, "end": v(108.75, 31.48) * mm});
            skLineSegment(sketch, "E292.1", {"start": v(108.75, 31.48) * mm, "end": v(112.42, 25.13) * mm});
            skLineSegment(sketch, "E292.2", {"start": v(112.42, 25.13) * mm, "end": v(108.75, 18.78) * mm});
            skLineSegment(sketch, "E292.3", {"start": v(108.75, 18.78) * mm, "end": v(101.42, 18.78) * mm});
            skLineSegment(sketch, "E292.4", {"start": v(101.42, 18.78) * mm, "end": v(97.76, 25.13) * mm});
            skLineSegment(sketch, "E292.5", {"start": v(97.76, 25.13) * mm, "end": v(101.42, 31.48) * mm});
            skPoint(sketch, "E292.0.midPoint", {"position": v(105.09, 31.48) * mm});
            skCircle(sketch, "E293.cCircle", {"center": v(102.8, 6.87) * mm, "radius": 3.17 * mm, "construction": true});
            skLineSegment(sketch, "E293.0", {"start": v(100.96, 10.04) * mm, "end": v(104.63, 10.04) * mm});
            skLineSegment(sketch, "E293.1", {"start": v(104.63, 10.04) * mm, "end": v(106.46, 6.87) * mm});
            skLineSegment(sketch, "E293.2", {"start": v(106.46, 6.87) * mm, "end": v(104.63, 3.7) * mm});
            skLineSegment(sketch, "E293.3", {"start": v(104.63, 3.7) * mm, "end": v(100.96, 3.7) * mm});
            skLineSegment(sketch, "E293.4", {"start": v(100.96, 3.7) * mm, "end": v(99.13, 6.87) * mm});
            skLineSegment(sketch, "E293.5", {"start": v(99.13, 6.87) * mm, "end": v(100.96, 10.04) * mm});
            skPoint(sketch, "E293.0.midPoint", {"position": v(102.8, 10.04) * mm});
            skCircle(sketch, "E294.cCircle", {"center": v(96.38, 10.04) * mm, "radius": 3.97 * mm, "construction": true});
            skLineSegment(sketch, "E294.0", {"start": v(94.09, 14.01) * mm, "end": v(98.67, 14.01) * mm});
            skLineSegment(sketch, "E294.1", {"start": v(98.67, 14.01) * mm, "end": v(100.96, 10.04) * mm});
            skLineSegment(sketch, "E294.2", {"start": v(100.96, 10.04) * mm, "end": v(98.67, 6.08) * mm});
            skLineSegment(sketch, "E294.3", {"start": v(98.67, 6.08) * mm, "end": v(94.09, 6.08) * mm});
            skLineSegment(sketch, "E294.4", {"start": v(94.09, 6.08) * mm, "end": v(91.8, 10.04) * mm});
            skLineSegment(sketch, "E294.5", {"start": v(91.8, 10.04) * mm, "end": v(94.09, 14.01) * mm});
            skPoint(sketch, "E294.0.midPoint", {"position": v(96.38, 14.01) * mm});
            skCircle(sketch, "E295.cCircle", {"center": v(95.92, 18.78) * mm, "radius": 4.76 * mm, "construction": true});
            skLineSegment(sketch, "E295.0", {"start": v(93.17, 23.54) * mm, "end": v(98.67, 23.54) * mm});
            skLineSegment(sketch, "E295.1", {"start": v(98.67, 23.54) * mm, "end": v(101.42, 18.78) * mm});
            skLineSegment(sketch, "E295.2", {"start": v(101.42, 18.78) * mm, "end": v(98.67, 14.01) * mm});
            skLineSegment(sketch, "E295.3", {"start": v(98.67, 14.01) * mm, "end": v(93.17, 14.01) * mm});
            skLineSegment(sketch, "E295.4", {"start": v(93.17, 14.01) * mm, "end": v(90.42, 18.78) * mm});
            skLineSegment(sketch, "E295.5", {"start": v(90.42, 18.78) * mm, "end": v(93.17, 23.54) * mm});
            skPoint(sketch, "E295.0.midPoint", {"position": v(95.92, 23.54) * mm});
            skLineSegment(sketch, "E296.top", {"start": v(-45.86, -51.99) * mm, "end": v(-45.64, -51.99) * mm});
            skPoint(sketch, "E297.visualSharp", {"position": v(-52.21, -51.99) * mm});
            skLineSegment(sketch, "E298.2", {"start": v(-39.47, -41.7) * mm, "end": v(-41.76, -45.67) * mm});
            skLineSegment(sketch, "E298.3", {"start": v(-41.76, -45.67) * mm, "end": v(-42.68, -45.67) * mm});
            skLineSegment(sketch, "E298.4", {"start": v(-48.18, -42.5) * mm, "end": v(-48.63, -41.7) * mm});
            skLineSegment(sketch, "E298.5", {"start": v(-48.63, -41.7) * mm, "end": v(-46.34, -37.73) * mm});
            skLineSegment(sketch, "E299.2", {"start": v(-42.68, -45.67) * mm, "end": v(-44.51, -48.85) * mm});
            skLineSegment(sketch, "E299.3", {"start": v(-44.51, -48.85) * mm, "end": v(-48.18, -48.85) * mm});
            skLineSegment(sketch, "E299.4", {"start": v(-48.18, -48.85) * mm, "end": v(-50, -45.67) * mm});
            skLineSegment(sketch, "E299.5", {"start": v(-50, -45.67) * mm, "end": v(-48.18, -42.5) * mm});
            skLineSegment(sketch, "E300.2", {"start": v(-53.5, -10.21) * mm, "end": v(-56.25, -14.97) * mm});
            skLineSegment(sketch, "E300.3", {"start": v(-56.25, -14.97) * mm, "end": v(-57.17, -14.97) * mm});
            skLineSegment(sketch, "E300.4", {"start": v(-64.05, -11) * mm, "end": v(-64.5, -10.21) * mm});
            skLineSegment(sketch, "E300.5", {"start": v(-64.5, -10.21) * mm, "end": v(-61.75, -5.45) * mm});
            skPoint(sketch, "E300.0.midPoint", {"position": v(-59, -5.45) * mm});
            skPoint(sketch, "E301.visualSharp", {"position": v(-69.91, -25.26) * mm});
            skLineSegment(sketch, "E302.2", {"start": v(-57.17, -14.97) * mm, "end": v(-59.46, -18.94) * mm});
            skLineSegment(sketch, "E302.3", {"start": v(-59.46, -18.94) * mm, "end": v(-60.38, -18.94) * mm});
            skLineSegment(sketch, "E302.4", {"start": v(-65.88, -15.77) * mm, "end": v(-66.34, -14.97) * mm});
            skLineSegment(sketch, "E302.5", {"start": v(-66.34, -14.97) * mm, "end": v(-64.05, -11) * mm});
            skPoint(sketch, "E302.0.midPoint", {"position": v(-61.75, -11) * mm});
            skLineSegment(sketch, "E303.2", {"start": v(-60.38, -18.94) * mm, "end": v(-62.21, -22.12) * mm});
            skLineSegment(sketch, "E303.3", {"start": v(-62.21, -22.12) * mm, "end": v(-65.88, -22.12) * mm});
            skLineSegment(sketch, "E303.4", {"start": v(-65.88, -22.12) * mm, "end": v(-67.71, -18.94) * mm});
            skLineSegment(sketch, "E303.5", {"start": v(-67.71, -18.94) * mm, "end": v(-65.88, -15.77) * mm});
            skPoint(sketch, "E303.0.midPoint", {"position": v(-64.05, -15.77) * mm});
            skPoint(sketch, "E304.orphan", {"position": v(-59, -10.21) * mm});
            skPoint(sketch, "E305.orphan", {"position": v(-61.75, -14.97) * mm});
            skPoint(sketch, "E306.orphan", {"position": v(-64.05, -18.94) * mm});
            const initialGuessF0  = {"E80": [-0.01362, -0.02397, 0, 1, 0.01006]};
            skSetInitialGuess(sketch, initialGuessF0);
            skSolve(sketch);
        }
        {
            var Q0;
            Q0 = qSketchRegion(id + "F0", true);
            extrude(context, id + "F1", {"entities" : qUnion([Q0]), "depth" : 3.17 * mm, "offsetDistance" : 25.4 * mm});
        }
        {
            var Q0;
            Q0=makeQuery(id+"F1.opExtrude","SWEPT_EDGE",EDGE,{"disambiguationData":[OSD([sQuery(id+"F0.wireOp",EDGE,"E3.filletArc"),sQuery(id+"F0.wireOp",EDGE,"KwcFEo9U-bClh-D8h3-GzTv-NhEbKNvI21TT")])]});
            var Q1;
            Q1=makeQuery(id+"F1.opExtrude","SWEPT_EDGE",EDGE,{"disambiguationData":[OSD([sQuery(id+"F0.wireOp",EDGE,"E7MvMFNV-uK8b-8ZiQ-7Duk-cUjbGVXh6u7s"),sQuery(id+"F0.wireOp",EDGE,"0ab612f3-548e-47c6-a8b8-d151de601088.trimOffspring")])]});
            var Q2;
            Q2=makeQuery(id+"F1.opExtrude","SWEPT_EDGE",EDGE,{"disambiguationData":[OSD([sQuery(id+"F0.wireOp",EDGE,"MFMcjicZ-tfMV-cnA4-Z9pC-shCIlQqRngmt"),sQuery(id+"F0.wireOp",EDGE,"49b1c2fe-dd47-4412-b7ba-a2595802a9c0.trimOffspring")])]});
            var Q3;
            Q3=makeQuery(id+"F1.opExtrude","SWEPT_EDGE",EDGE,{"disambiguationData":[OSD([sQuery(id+"F0.wireOp",EDGE,"hqcUmv8U-3Y2f-1DYb-XFRx-DoM0Ldty7pgK"),sQuery(id+"F0.wireOp",EDGE,"0ab612f3-548e-47c6-a8b8-d151de601088.trimOffspring")])]});
            var Q4;
            Q4=makeQuery(id+"F1.opExtrude","SWEPT_EDGE",EDGE,{"disambiguationData":[OSD([sQuery(id+"F0.wireOp",EDGE,"BDxbyBsN-WUfq-DDqC-Ylty-fahBLUCrJihu"),sQuery(id+"F0.wireOp",EDGE,"49b1c2fe-dd47-4412-b7ba-a2595802a9c0.trimOffspring")])]});
            var Q5;
            Q5=makeQuery(id+"F1.opExtrude","SWEPT_EDGE",EDGE,{"disambiguationData":[OSD([sQuery(id+"F0.wireOp",EDGE,"qLwkn0zT-rJZj-oCyo-4JJa-DjERWgxp8KWt"),sQuery(id+"F0.wireOp",EDGE,"457cc2dd-0a22-47f4-a5e9-31956becaa98.trimOffspring")])]});
            var Q6;
            Q6=makeQuery(id+"F1.opExtrude","SWEPT_EDGE",EDGE,{"disambiguationData":[OSD([sQuery(id+"F0.wireOp",EDGE,"QbkmLgDQ-2k58-Ziiz-fUbB-J4hHGqKfhEZH"),sQuery(id+"F0.wireOp",EDGE,"6d273b1b-6e05-4ff9-b154-a73bd32e1f71.trimOffspring")])]});
            var Q7;
            Q7=makeQuery(id+"F1.opExtrude","SWEPT_EDGE",EDGE,{"disambiguationData":[OSD([sQuery(id+"F0.wireOp",EDGE,"QKDGq1wy-vTCk-Lj4D-VITr-jcaQ08ZgOf7o"),sQuery(id+"F0.wireOp",EDGE,"1e7fb99e-4ad8-4cc2-a7fa-02e236824d87.trimOffspring")])]});
            var Q8;
            Q8=makeQuery(id+"F1.opExtrude","SWEPT_EDGE",EDGE,{"disambiguationData":[OSD([sQuery(id+"F0.wireOp",EDGE,"cXYAuPDi-3OGr-QPoA-gxEK-N9iT9CviMBYx"),sQuery(id+"F0.wireOp",EDGE,"49480ebe-8ed0-4ae2-94ab-956c5f313c19.trimOffspring")])]});
            var Q9;
            Q9=makeQuery(id+"F1.opExtrude","SWEPT_EDGE",EDGE,{"disambiguationData":[OSD([sQuery(id+"F0.wireOp",EDGE,"hI7Z9iwd-lZgc-Dfsw-L6mG-scNOy0WF6EC7"),sQuery(id+"F0.wireOp",EDGE,"2a180a66-34a1-4841-8f87-04e5eba1ceab.trimOffspring")])]});
            var Q10;
            Q10=makeQuery(id+"F1.opExtrude","SWEPT_EDGE",EDGE,{"disambiguationData":[OSD([sQuery(id+"F0.wireOp",EDGE,"c8rfMAqR-dkwd-qCW3-9neE-H0AE0oPbs4Qp"),sQuery(id+"F0.wireOp",EDGE,"401ab048-5759-4413-abed-1134ba47fddd.trimOffspring")])]});
            var Q11;
            Q11=makeQuery(id+"F1.opExtrude","SWEPT_EDGE",EDGE,{"disambiguationData":[OSD([sQuery(id+"F0.wireOp",EDGE,"XWb4HBB5-t2Hc-oUr3-o6c1-bTJZQE5nsMn5"),sQuery(id+"F0.wireOp",EDGE,"39d9c749-9ffb-4b8e-ae83-386e5194df48.trimOffspring")])]});
            var Q12;
            Q12=makeQuery(id+"F1.opExtrude","SWEPT_EDGE",EDGE,{"disambiguationData":[OSD([sQuery(id+"F0.wireOp",EDGE,"BWBwDpZV-HqS4-YjK9-sSWS-v8iRheQrnra1"),sQuery(id+"F0.wireOp",EDGE,"fe6c2a4a-91f1-4b4e-b1e2-6b86066d8226.trimOffspring")])]});
            var Q13;
            Q13=makeQuery(id+"F1.opExtrude","SWEPT_EDGE",EDGE,{"disambiguationData":[OSD([sQuery(id+"F0.wireOp",EDGE,"DpMHMzxM-oLeH-X24q-mFt2-Zfh6rWlBPqLy"),sQuery(id+"F0.wireOp",EDGE,"e7940485-faa3-4b5d-8451-879a44a0535b.trimOffspring")])]});
            var Q14;
            Q14=makeQuery(id+"F1.opExtrude","SWEPT_EDGE",EDGE,{"disambiguationData":[OSD([sQuery(id+"F0.wireOp",EDGE,"8p8z02rz-XM1F-gFPC-RQVa-rfRN30CTPnuF"),sQuery(id+"F0.wireOp",EDGE,"cf35a97e-a59c-43df-8749-063313af8aeb.trimOffspring")])]});
            var Q15;
            Q15=makeQuery(id+"F1.opExtrude","SWEPT_EDGE",EDGE,{"disambiguationData":[OSD([sQuery(id+"F0.wireOp",EDGE,"1KdZPy54-IAHz-HdOO-9pBj-XyZoVR0dbeO1"),sQuery(id+"F0.wireOp",EDGE,"4941a0d5-5b4d-4c2d-bee2-9b9f4ed584f5.trimOffspring")])]});
            var Q16;
            Q16=makeQuery(id+"F1.opExtrude","SWEPT_EDGE",EDGE,{"disambiguationData":[OSD([sQuery(id+"F0.wireOp",EDGE,"D77W7Ugb-ZPTO-vBp9-5ZPV-knq85JaC9yaM"),sQuery(id+"F0.wireOp",EDGE,"105bb943-4d21-436c-ae5a-a526161733bb.trimOffspring")])]});
            var Q17;
            Q17=makeQuery(id+"F1.opExtrude","SWEPT_EDGE",EDGE,{"disambiguationData":[OSD([sQuery(id+"F0.wireOp",EDGE,"E0.right"),sQuery(id+"F0.wireOp",EDGE,"itbIzTSW-YEBt-L2aj-MggJ-UpqGRpPm7y69")])]});
            var Q18;
            Q18=makeQuery(id+"F1.opExtrude","SWEPT_EDGE",EDGE,{"disambiguationData":[OSD([sQuery(id+"F0.wireOp",EDGE,"KvrqN5Q7-6TQ0-ukyS-9HFH-Bqw6vbqitdDL"),sQuery(id+"F0.wireOp",EDGE,"457cc2dd-0a22-47f4-a5e9-31956becaa98.trimOffspring")])]});
            var Q19;
            Q19=makeQuery(id+"F1.opExtrude","SWEPT_EDGE",EDGE,{"disambiguationData":[OSD([sQuery(id+"F0.wireOp",EDGE,"92eDQtEN-0jaI-xoSh-TXxB-fUASiIEMQFeJ"),sQuery(id+"F0.wireOp",EDGE,"6d273b1b-6e05-4ff9-b154-a73bd32e1f71.trimOffspring")])]});
            var Q20;
            Q20=makeQuery(id+"F1.opExtrude","SWEPT_EDGE",EDGE,{"disambiguationData":[OSD([sQuery(id+"F0.wireOp",EDGE,"5c0QZ8NB-kqrX-tXYX-rwGu-YhZIMP3kNjtv"),sQuery(id+"F0.wireOp",EDGE,"1e7fb99e-4ad8-4cc2-a7fa-02e236824d87.trimOffspring")])]});
            var Q21;
            Q21=makeQuery(id+"F1.opExtrude","SWEPT_EDGE",EDGE,{"disambiguationData":[OSD([sQuery(id+"F0.wireOp",EDGE,"Co8MspyC-jpgy-OqRi-9X62-KS5NYQvcvOHt"),sQuery(id+"F0.wireOp",EDGE,"49480ebe-8ed0-4ae2-94ab-956c5f313c19.trimOffspring")])]});
            var Q22;
            Q22=makeQuery(id+"F1.opExtrude","SWEPT_EDGE",EDGE,{"disambiguationData":[OSD([sQuery(id+"F0.wireOp",EDGE,"N0CfcBmX-WNQ3-BAAi-rMmY-l0h40gDwQezy"),sQuery(id+"F0.wireOp",EDGE,"2a180a66-34a1-4841-8f87-04e5eba1ceab.trimOffspring")])]});
            var Q23;
            Q23=makeQuery(id+"F1.opExtrude","SWEPT_EDGE",EDGE,{"disambiguationData":[OSD([sQuery(id+"F0.wireOp",EDGE,"frJKysNw-LHww-dgYr-2R5g-6tPWvze6kZkP"),sQuery(id+"F0.wireOp",EDGE,"401ab048-5759-4413-abed-1134ba47fddd.trimOffspring")])]});
            var Q24;
            Q24=makeQuery(id+"F1.opExtrude","SWEPT_EDGE",EDGE,{"disambiguationData":[OSD([sQuery(id+"F0.wireOp",EDGE,"ioAGfyNb-zQ6n-KKhh-X4Rq-4gnoXz22f1pc"),sQuery(id+"F0.wireOp",EDGE,"39d9c749-9ffb-4b8e-ae83-386e5194df48.trimOffspring")])]});
            var Q25;
            Q25=makeQuery(id+"F1.opExtrude","SWEPT_EDGE",EDGE,{"disambiguationData":[OSD([sQuery(id+"F0.wireOp",EDGE,"4Z05me6M-pVjN-uT1z-6B9z-4clwtVMk1WCp"),sQuery(id+"F0.wireOp",EDGE,"fe6c2a4a-91f1-4b4e-b1e2-6b86066d8226.trimOffspring")])]});
            var Q26;
            Q26=makeQuery(id+"F1.opExtrude","SWEPT_EDGE",EDGE,{"disambiguationData":[OSD([sQuery(id+"F0.wireOp",EDGE,"CTEV1Vwn-BGBE-jlHb-FHnF-PdhdXIVbAuRO"),sQuery(id+"F0.wireOp",EDGE,"e7940485-faa3-4b5d-8451-879a44a0535b.trimOffspring")])]});
            var Q27;
            Q27=makeQuery(id+"F1.opExtrude","SWEPT_EDGE",EDGE,{"disambiguationData":[OSD([sQuery(id+"F0.wireOp",EDGE,"vmLdqNc3-eLYz-mePX-fzRX-2egRdkYDBIuf"),sQuery(id+"F0.wireOp",EDGE,"cf35a97e-a59c-43df-8749-063313af8aeb.trimOffspring")])]});
            var Q28;
            Q28=makeQuery(id+"F1.opExtrude","SWEPT_EDGE",EDGE,{"disambiguationData":[OSD([sQuery(id+"F0.wireOp",EDGE,"uBCBu26M-MPGh-sdtj-RZAV-gj2qaw1dCL6s"),sQuery(id+"F0.wireOp",EDGE,"4941a0d5-5b4d-4c2d-bee2-9b9f4ed584f5.trimOffspring")])]});
            var Q29;
            Q29=makeQuery(id+"F1.opExtrude","SWEPT_EDGE",EDGE,{"disambiguationData":[OSD([sQuery(id+"F0.wireOp",EDGE,"AOzfUuVY-sAip-yR5B-ZQbZ-Zymy6F6M52jt"),sQuery(id+"F0.wireOp",EDGE,"105bb943-4d21-436c-ae5a-a526161733bb.trimOffspring")])]});
            fillet(context, id + "F2", {"entities" : qUnion([Q0, Q1, Q2, Q3, Q4, Q5, Q6, Q7, Q8, Q9, Q10, Q11, Q12, Q13, Q14, Q15, Q16, Q17, Q18, Q19, Q20, Q21, Q22, Q23, Q24, Q25, Q26, Q27, Q28, Q29]), "radius" : 0.5 * mm, "tangentPropagation" : true, "allowEdgeOverflow" : false});
        }
        {
            var Q0;
            Q0=makeQuery(id+"F1.opExtrude","CAP_EDGE",EDGE,{"disambiguationData":[OSD([sQuery(id+"F0.wireOp",EDGE,"E18")])],"isStart":false});
            var Q1;
            Q1=makeQuery(id+"F1.opExtrude","CAP_EDGE",EDGE,{"disambiguationData":[OSD([sQuery(id+"F0.wireOp",EDGE,"E211.trimOffspring")])],"isStart":false});
            var Q2;
            Q2=makeQuery(id+"F1.opExtrude","CAP_EDGE",EDGE,{"disambiguationData":[OSD([sQuery(id+"F0.wireOp",EDGE,"E213.trimOffspring")])],"isStart":false});
            var Q3;
            Q3=makeQuery(id+"F1.opExtrude","CAP_EDGE",EDGE,{"disambiguationData":[OSD([sQuery(id+"F0.wireOp",EDGE,"E16")])],"isStart":false});
            var Q4;
            Q4=makeQuery(id+"F1.opExtrude","CAP_EDGE",EDGE,{"disambiguationData":[OSD([sQuery(id+"F0.wireOp",EDGE,"E207.trimOffspring")])],"isStart":false});
            var Q5;
            Q5=makeQuery(id+"F1.opExtrude","CAP_EDGE",EDGE,{"disambiguationData":[OSD([sQuery(id+"F0.wireOp",EDGE,"E202.trimOffspring")])],"isStart":false});
            var Q6;
            Q6=makeQuery(id+"F1.opExtrude","CAP_EDGE",EDGE,{"disambiguationData":[OSD([sQuery(id+"F0.wireOp",EDGE,"E6"),sQuery(id+"F0.wireOp",EDGE,"E204")])],"isStart":true});
            var Q7;
            Q7=makeQuery(id+"F1.opExtrude","CAP_EDGE",EDGE,{"disambiguationData":[OSD([sQuery(id+"F0.wireOp",EDGE,"E193.trimOffspring"),sQuery(id+"F0.wireOp",EDGE,"E212.trimOffspring")])],"isStart":true});
            var Q8;
            Q8=makeQuery(id+"F1.opExtrude","CAP_EDGE",EDGE,{"disambiguationData":[OSD([sQuery(id+"F0.wireOp",EDGE,"E195.trimOffspring"),sQuery(id+"F0.wireOp",EDGE,"E197")])],"isStart":true});
            var Q9;
            Q9=makeQuery(id+"F1.opExtrude","CAP_EDGE",EDGE,{"disambiguationData":[OSD([sQuery(id+"F0.wireOp",EDGE,"E9.MirrorCS"),sQuery(id+"F0.wireOp",EDGE,"E200.trimOffspring")])],"isStart":true});
            var Q10;
            Q10=makeQuery(id+"F1.opExtrude","CAP_EDGE",EDGE,{"disambiguationData":[OSD([sQuery(id+"F0.wireOp",EDGE,"E207.trimOffspring")])],"isStart":true});
            var Q11;
            Q11=makeQuery(id+"F1.opExtrude","CAP_EDGE",EDGE,{"disambiguationData":[OSD([sQuery(id+"F0.wireOp",EDGE,"E16")])],"isStart":true});
            var Q12;
            Q12=makeQuery(id+"F1.opExtrude","CAP_EDGE",EDGE,{"disambiguationData":[OSD([sQuery(id+"F0.wireOp",EDGE,"E202.trimOffspring")])],"isStart":true});
            var Q13;
            Q13=makeQuery(id+"F1.opExtrude","CAP_EDGE",EDGE,{"disambiguationData":[OSD([sQuery(id+"F0.wireOp",EDGE,"E18")])],"isStart":true});
            var Q14;
            Q14=makeQuery(id+"F1.opExtrude","CAP_EDGE",EDGE,{"disambiguationData":[OSD([sQuery(id+"F0.wireOp",EDGE,"E211.trimOffspring")])],"isStart":true});
            var Q15;
            Q15=makeQuery(id+"F1.opExtrude","CAP_EDGE",EDGE,{"disambiguationData":[OSD([sQuery(id+"F0.wireOp",EDGE,"E213.trimOffspring")])],"isStart":true});
            var Q16;
            Q16=makeQuery(id+"F1.opExtrude","CAP_EDGE",EDGE,{"disambiguationData":[OSD([sQuery(id+"F0.wireOp",EDGE,"E193.trimOffspring"),sQuery(id+"F0.wireOp",EDGE,"E212.trimOffspring")])],"isStart":false});
            var Q17;
            Q17=makeQuery(id+"F1.opExtrude","CAP_EDGE",EDGE,{"disambiguationData":[OSD([sQuery(id+"F0.wireOp",EDGE,"E6"),sQuery(id+"F0.wireOp",EDGE,"E204")])],"isStart":false});
            var Q18;
            Q18=makeQuery(id+"F1.opExtrude","CAP_EDGE",EDGE,{"disambiguationData":[OSD([sQuery(id+"F0.wireOp",EDGE,"E195.trimOffspring"),sQuery(id+"F0.wireOp",EDGE,"E197")])],"isStart":false});
            var Q19;
            Q19=makeQuery(id+"F1.opExtrude","CAP_EDGE",EDGE,{"disambiguationData":[OSD([sQuery(id+"F0.wireOp",EDGE,"E9.MirrorCS"),sQuery(id+"F0.wireOp",EDGE,"E200.trimOffspring")])],"isStart":false});
            fillet(context, id + "F3", {"entities" : qUnion([Q0, Q1, Q2, Q3, Q4, Q5, Q6, Q7, Q8, Q9, Q10, Q11, Q12, Q13, Q14, Q15, Q16, Q17, Q18, Q19]), "radius" : 0.5 * mm, "tangentPropagation" : true, "allowEdgeOverflow" : false});
        }
        {
            var Q0;
            Q0=makeQuery(id+"F1.opExtrude","CAP_FACE",FACE,{"disambiguationData":[OSD([sQuery(id+"F0.wireOp",EDGE,"E0.bottom"),sQuery(id+"F0.wireOp",EDGE,"E0.top"),sQuery(id+"F0.wireOp",EDGE,"E0.left"),sQuery(id+"F0.wireOp",EDGE,"E0.right"),sQuery(id+"F0.wireOp",EDGE,"E1.filletArc"),sQuery(id+"F0.wireOp",EDGE,"E2.filletArc"),sQuery(id+"F0.wireOp",EDGE,"E3.filletArc"),sQuery(id+"F0.wireOp",EDGE,"E4.filletArc"),sQuery(id+"F0.wireOp",EDGE,"E5"),sQuery(id+"F0.wireOp",EDGE,"E6"),sQuery(id+"F0.wireOp",EDGE,"E7"),sQuery(id+"F0.wireOp",EDGE,"E8.MirrorCS"),sQuery(id+"F0.wireOp",EDGE,"E9.MirrorCS"),sQuery(id+"F0.wireOp",EDGE,"E10.MirrorCS"),sQuery(id+"F0.wireOp",EDGE,"E16"),sQuery(id+"F0.wireOp",EDGE,"E18"),sQuery(id+"F0.wireOp",EDGE,"E19.trimOffspring"),sQuery(id+"F0.wireOp",EDGE,"E22.MirrorCS"),sQuery(id+"F0.wireOp",EDGE,"E23"),sQuery(id+"F0.wireOp",EDGE,"E26.MirrorCS"),sQuery(id+"F0.wireOp",EDGE,"E27"),sQuery(id+"F0.wireOp",EDGE,"E28"),sQuery(id+"F0.wireOp",EDGE,"E29"),sQuery(id+"F0.wireOp",EDGE,"E30"),sQuery(id+"F0.wireOp",EDGE,"E31"),sQuery(id+"F0.wireOp",EDGE,"E32"),sQuery(id+"F0.wireOp",EDGE,"E33"),sQuery(id+"F0.wireOp",EDGE,"E34"),sQuery(id+"F0.wireOp",EDGE,"E35"),sQuery(id+"F0.wireOp",EDGE,"E36"),sQuery(id+"F0.wireOp",EDGE,"E37"),sQuery(id+"F0.wireOp",EDGE,"E38"),sQuery(id+"F0.wireOp",EDGE,"E39"),sQuery(id+"F0.wireOp",EDGE,"E42.trimOffspring"),sQuery(id+"F0.wireOp",EDGE,"E43"),sQuery(id+"F0.wireOp",EDGE,"E45.trimOffspring"),sQuery(id+"F0.wireOp",EDGE,"E46.trimOffspring"),sQuery(id+"F0.wireOp",EDGE,"E49.MirrorCS"),sQuery(id+"F0.wireOp",EDGE,"E50.MirrorCS"),sQuery(id+"F0.wireOp",EDGE,"E51.MirrorCS"),sQuery(id+"F0.wireOp",EDGE,"E52.MirrorCS"),sQuery(id+"F0.wireOp",EDGE,"E53.MirrorCS"),sQuery(id+"F0.wireOp",EDGE,"E54.MirrorCS"),sQuery(id+"F0.wireOp",EDGE,"E55.MirrorCS"),sQuery(id+"F0.wireOp",EDGE,"E56.MirrorCS"),sQuery(id+"F0.wireOp",EDGE,"E57.MirrorCS"),sQuery(id+"F0.wireOp",EDGE,"E58.MirrorCS"),sQuery(id+"F0.wireOp",EDGE,"E59.MirrorCS"),sQuery(id+"F0.wireOp",EDGE,"E60.MirrorCS"),sQuery(id+"F0.wireOp",EDGE,"E61.MirrorCS"),sQuery(id+"F0.wireOp",EDGE,"E62.MirrorCS"),sQuery(id+"F0.wireOp",EDGE,"E63.MirrorCS"),sQuery(id+"F0.wireOp",EDGE,"E64.MirrorCS"),sQuery(id+"F0.wireOp",EDGE,"E65.MirrorCS"),sQuery(id+"F0.wireOp",EDGE,"E67.0"),sQuery(id+"F0.wireOp",EDGE,"E68.0"),sQuery(id+"F0.wireOp",EDGE,"E69.trimOffspring"),sQuery(id+"F0.wireOp",EDGE,"E71.trimOffspring"),sQuery(id+"F0.wireOp",EDGE,"E76.trimOffspring"),sQuery(id+"F0.wireOp",EDGE,"E77.trimOffspring"),sQuery(id+"F0.wireOp",EDGE,"E78.trimOffspring"),sQuery(id+"F0.wireOp",EDGE,"E79.trimOffspring"),sQuery(id+"F0.wireOp",EDGE,"E80.sketch_text.stroke-0"),sQuery(id+"F0.wireOp",EDGE,"E80.sketch_text.stroke-1"),sQuery(id+"F0.wireOp",EDGE,"E80.sketch_text.stroke-2"),sQuery(id+"F0.wireOp",EDGE,"E80.sketch_text.stroke-3"),sQuery(id+"F0.wireOp",EDGE,"E80.sketch_text.stroke-4"),sQuery(id+"F0.wireOp",EDGE,"E80.sketch_text.stroke-5"),sQuery(id+"F0.wireOp",EDGE,"E80.sketch_text.stroke-6"),sQuery(id+"F0.wireOp",EDGE,"E80.sketch_text.stroke-7"),sQuery(id+"F0.wireOp",EDGE,"E80.sketch_text.stroke-8"),sQuery(id+"F0.wireOp",EDGE,"E80.sketch_text.stroke-9"),sQuery(id+"F0.wireOp",EDGE,"E80.sketch_text.stroke-10"),sQuery(id+"F0.wireOp",EDGE,"E80.sketch_text.stroke-11"),sQuery(id+"F0.wireOp",EDGE,"E81"),sQuery(id+"F0.wireOp",EDGE,"E82"),sQuery(id+"F0.wireOp",EDGE,"E83"),sQuery(id+"F0.wireOp",EDGE,"E84"),sQuery(id+"F0.wireOp",EDGE,"E85"),sQuery(id+"F0.wireOp",EDGE,"E87"),sQuery(id+"F0.wireOp",EDGE,"E88"),sQuery(id+"F0.wireOp",EDGE,"E89"),sQuery(id+"F0.wireOp",EDGE,"E90"),sQuery(id+"F0.wireOp",EDGE,"E91"),sQuery(id+"F0.wireOp",EDGE,"E93"),sQuery(id+"F0.wireOp",EDGE,"E94"),sQuery(id+"F0.wireOp",EDGE,"E95"),sQuery(id+"F0.wireOp",EDGE,"E96"),sQuery(id+"F0.wireOp",EDGE,"E97"),sQuery(id+"F0.wireOp",EDGE,"E98"),sQuery(id+"F0.wireOp",EDGE,"E99"),sQuery(id+"F0.wireOp",EDGE,"E100"),sQuery(id+"F0.wireOp",EDGE,"E101"),sQuery(id+"F0.wireOp",EDGE,"79a4f8d0-de25-4821-8878-42326f9d03c0"),sQuery(id+"F0.wireOp",EDGE,"E102"),sQuery(id+"F0.wireOp",EDGE,"E103"),sQuery(id+"F0.wireOp",EDGE,"E104"),sQuery(id+"F0.wireOp",EDGE,"E105"),sQuery(id+"F0.wireOp",EDGE,"E106"),sQuery(id+"F0.wireOp",EDGE,"E107"),sQuery(id+"F0.wireOp",EDGE,"E108"),sQuery(id+"F0.wireOp",EDGE,"E109"),sQuery(id+"F0.wireOp",EDGE,"E110"),sQuery(id+"F0.wireOp",EDGE,"E111"),sQuery(id+"F0.wireOp",EDGE,"E112"),sQuery(id+"F0.wireOp",EDGE,"E113"),sQuery(id+"F0.wireOp",EDGE,"E115"),sQuery(id+"F0.wireOp",EDGE,"E116"),sQuery(id+"F0.wireOp",EDGE,"E117"),sQuery(id+"F0.wireOp",EDGE,"E114"),sQuery(id+"F0.wireOp",EDGE,"E118"),sQuery(id+"F0.wireOp",EDGE,"E119"),sQuery(id+"F0.wireOp",EDGE,"E120"),sQuery(id+"F0.wireOp",EDGE,"E121"),sQuery(id+"F0.wireOp",EDGE,"E123"),sQuery(id+"F0.wireOp",EDGE,"E124"),sQuery(id+"F0.wireOp",EDGE,"E125"),sQuery(id+"F0.wireOp",EDGE,"E122"),sQuery(id+"F0.wireOp",EDGE,"E126"),sQuery(id+"F0.wireOp",EDGE,"E127"),sQuery(id+"F0.wireOp",EDGE,"E128"),sQuery(id+"F0.wireOp",EDGE,"E129"),sQuery(id+"F0.wireOp",EDGE,"E131"),sQuery(id+"F0.wireOp",EDGE,"E132"),sQuery(id+"F0.wireOp",EDGE,"E133"),sQuery(id+"F0.wireOp",EDGE,"E130"),sQuery(id+"F0.wireOp",EDGE,"E134"),sQuery(id+"F0.wireOp",EDGE,"E135"),sQuery(id+"F0.wireOp",EDGE,"E136"),sQuery(id+"F0.wireOp",EDGE,"E137"),sQuery(id+"F0.wireOp",EDGE,"E139"),sQuery(id+"F0.wireOp",EDGE,"E140"),sQuery(id+"F0.wireOp",EDGE,"E141"),sQuery(id+"F0.wireOp",EDGE,"E138"),sQuery(id+"F0.wireOp",EDGE,"E142"),sQuery(id+"F0.wireOp",EDGE,"E143"),sQuery(id+"F0.wireOp",EDGE,"E144"),sQuery(id+"F0.wireOp",EDGE,"E145"),sQuery(id+"F0.wireOp",EDGE,"E146.0"),sQuery(id+"F0.wireOp",EDGE,"E147.0"),sQuery(id+"F0.wireOp",EDGE,"E148.0"),sQuery(id+"F0.wireOp",EDGE,"E149.0"),sQuery(id+"F0.wireOp",EDGE,"E150"),sQuery(id+"F0.wireOp",EDGE,"E151"),sQuery(id+"F0.wireOp",EDGE,"E152"),sQuery(id+"F0.wireOp",EDGE,"E153"),sQuery(id+"F0.wireOp",EDGE,"E154"),sQuery(id+"F0.wireOp",EDGE,"E155"),sQuery(id+"F0.wireOp",EDGE,"E156"),sQuery(id+"F0.wireOp",EDGE,"E157"),sQuery(id+"F0.wireOp",EDGE,"E158"),sQuery(id+"F0.wireOp",EDGE,"E159"),sQuery(id+"F0.wireOp",EDGE,"E160"),sQuery(id+"F0.wireOp",EDGE,"E161"),sQuery(id+"F0.wireOp",EDGE,"E162"),sQuery(id+"F0.wireOp",EDGE,"E163"),sQuery(id+"F0.wireOp",EDGE,"E164"),sQuery(id+"F0.wireOp",EDGE,"E165"),sQuery(id+"F0.wireOp",EDGE,"E166"),sQuery(id+"F0.wireOp",EDGE,"E167"),sQuery(id+"F0.wireOp",EDGE,"E168"),sQuery(id+"F0.wireOp",EDGE,"E169"),sQuery(id+"F0.wireOp",EDGE,"E170"),sQuery(id+"F0.wireOp",EDGE,"E171"),sQuery(id+"F0.wireOp",EDGE,"E172.trimOffspring"),sQuery(id+"F0.wireOp",EDGE,"E173.trimOffspring"),sQuery(id+"F0.wireOp",EDGE,"E174.trimOffspring"),sQuery(id+"F0.wireOp",EDGE,"E175.trimOffspring"),sQuery(id+"F0.wireOp",EDGE,"E176.trimOffspring"),sQuery(id+"F0.wireOp",EDGE,"E177.trimOffspring"),sQuery(id+"F0.wireOp",EDGE,"E178.trimOffspring"),sQuery(id+"F0.wireOp",EDGE,"E179.trimOffspring"),sQuery(id+"F0.wireOp",EDGE,"E180.trimOffspring"),sQuery(id+"F0.wireOp",EDGE,"E181.trimOffspring"),sQuery(id+"F0.wireOp",EDGE,"E182.trimOffspring"),sQuery(id+"F0.wireOp",EDGE,"E183.trimOffspring"),sQuery(id+"F0.wireOp",EDGE,"E184.trimOffspring"),sQuery(id+"F0.wireOp",EDGE,"E185.trimOffspring"),sQuery(id+"F0.wireOp",EDGE,"E186.trimOffspring"),sQuery(id+"F0.wireOp",EDGE,"E187.trimOffspring"),sQuery(id+"F0.wireOp",EDGE,"E188.trimOffspring"),sQuery(id+"F0.wireOp",EDGE,"E190"),sQuery(id+"F0.wireOp",EDGE,"E191"),sQuery(id+"F0.wireOp",EDGE,"E193.trimOffspring"),sQuery(id+"F0.wireOp",EDGE,"E195.trimOffspring"),sQuery(id+"F0.wireOp",EDGE,"E197"),sQuery(id+"F0.wireOp",EDGE,"E198"),sQuery(id+"F0.wireOp",EDGE,"E200.trimOffspring"),sQuery(id+"F0.wireOp",EDGE,"E202.trimOffspring"),sQuery(id+"F0.wireOp",EDGE,"E203.trimOffspring"),sQuery(id+"F0.wireOp",EDGE,"E204"),sQuery(id+"F0.wireOp",EDGE,"E207.trimOffspring"),sQuery(id+"F0.wireOp",EDGE,"E208.MirrorCS"),sQuery(id+"F0.wireOp",EDGE,"E209.MirrorCS"),sQuery(id+"F0.wireOp",EDGE,"E211.trimOffspring"),sQuery(id+"F0.wireOp",EDGE,"E212.trimOffspring"),sQuery(id+"F0.wireOp",EDGE,"E213.trimOffspring"),sQuery(id+"F0.wireOp",EDGE,"E214"),sQuery(id+"F0.wireOp",EDGE,"E215.0"),sQuery(id+"F0.wireOp",EDGE,"E216.MirrorCS"),sQuery(id+"F0.wireOp",EDGE,"E217.MirrorCS"),sQuery(id+"F0.wireOp",EDGE,"E218.MirrorCS"),sQuery(id+"F0.wireOp",EDGE,"E221.MirrorCS"),sQuery(id+"F0.wireOp",EDGE,"E223.0"),sQuery(id+"F0.wireOp",EDGE,"E224"),sQuery(id+"F0.wireOp",EDGE,"E225"),sQuery(id+"F0.wireOp",EDGE,"E226.MirrorCS"),sQuery(id+"F0.wireOp",EDGE,"E227.MirrorCS"),sQuery(id+"F0.wireOp",EDGE,"E228.MirrorCS"),sQuery(id+"F0.wireOp",EDGE,"E229"),sQuery(id+"F0.wireOp",EDGE,"E230.MirrorCS"),sQuery(id+"F0.wireOp",EDGE,"3dc38050-8edc-4d42-b04c-eaa21bf2e0a0.1"),sQuery(id+"F0.wireOp",EDGE,"e4574c0f-6a98-4f32-a32a-c108774d045c.0"),sQuery(id+"F0.wireOp",EDGE,"b95a71d1-bf8c-48bc-b8c3-2cf85ccb1f46.0"),sQuery(id+"F0.wireOp",EDGE,"6CdnfpsF-UXbz-2lWf-uGiN-xV6Clk6CIY2p"),sQuery(id+"F0.wireOp",EDGE,"KS5p9Uql-fqoi-JtGu-taWY-fYe7bwKlLbq6"),sQuery(id+"F0.wireOp",EDGE,"BpbhWuwh-fzUD-TgpT-2ZhU-je7DzOudBbx2"),sQuery(id+"F0.wireOp",EDGE,"R8LeVDRJ-FVDW-Pxxb-p9s3-yAxdAxvIfl0D"),sQuery(id+"F0.wireOp",EDGE,"u3q2aAR3-qywJ-678t-KDM3-BQjLNxFmgKIp"),sQuery(id+"F0.wireOp",EDGE,"1zP8rDmj-YOUN-6304-H82i-UbNZi5IW9xmn"),sQuery(id+"F0.wireOp",EDGE,"iAE1nxCd-g0cb-LlmT-wda9-sPFThKMbQK5z"),sQuery(id+"F0.wireOp",EDGE,"yTdGwwuI-YBCA-HG15-3odK-iPDKNbZLJZ6I"),sQuery(id+"F0.wireOp",EDGE,"Ms6NsYPA-J4kW-OH2l-AAyO-E9cR8JsWQ4yT"),sQuery(id+"F0.wireOp",EDGE,"WaIveHo5-VdCo-zpOC-L39Y-QGmYMk3Qi7xO")])],"isStart":false});
            var sketch = newSketch(context, id + "F4", { "sketchPlane" : qUnion([Q0])});
            skLineSegment(sketch, "E307.0", {"start": v(4.65, -40.26) * mm, "end": v(20.64, -40.26) * mm});
            skArc(sketch, "E308.0", {"start": v(-8.74, -45.01) * mm, "mid": v(-3.77, -45.27) * mm, "end": v(0.4, -42.58) * mm});
            skArc(sketch, "E309.0", {"start": v(20.64, -40.26) * mm, "mid": v(23.33, -39.14) * mm, "end": v(24.45, -36.45) * mm});
            skArc(sketch, "E310", {"start": v(4.65, -40.26) * mm, "mid": v(2.2, -41.12) * mm, "end": v(0.22, -42.8) * mm});
            skSolve(sketch);
        }
        {
            var Q0;
            Q0=makeQuery(id+"F1.opExtrude","SWEPT_FACE",FACE,{"disambiguationData":[OSD([sQuery(id+"F0.wireOp",EDGE,"E94")])]});
            var sketch = newSketch(context, id + "F5", { "sketchPlane" : qUnion([Q0])});
            skLineSegment(sketch, "E311", {"start": v(24.45, -3.18) * mm, "end": v(24.45, 0) * mm});
            skLineSegment(sketch, "E312", {"start": v(24.45, 0) * mm, "end": v(28.82, 0) * mm});
            skLineSegment(sketch, "E313", {"start": v(24.45, -3.18) * mm, "end": v(26.99, 0) * mm});
            skLineSegment(sketch, "E314", {"start": v(26.99, 0) * mm, "end": v(26.99, -3.18) * mm});
            skLineSegment(sketch, "E315", {"start": v(26.99, -3.18) * mm, "end": v(24.45, -3.18) * mm});
            skSolve(sketch);
        }
        {
            var Q0;
            {var subQ0=sQuery(id+"F5.wireOp",EDGE,"E314");Q0=makeQuery(id+"F5.imprint","IMPRINT",FACE,{"disambiguationData":[TD([[makeQuery(id+"F5.imprint","IMPRINT",EDGE,{"derivedFrom":subQ0}),-1.0]])]});}
            var Q1;
            {var subQ1=sQuery(id+"F5.wireOp",EDGE,"E313");var subQ2=sQuery(id+"F0.wireOp",EDGE,"E94");var subQ4=makeQuery(id+"F1.opExtrude","SWEPT_EDGE",EDGE,{"disambiguationData":[OSD([sQuery(id+"F0.wireOp",EDGE,"E91"),subQ2])]});var subQ5=makeQuery(id+"F5.imprint","INTERSECT",VERTEX,{"derivedFrom":[subQ4,subQ1]});Q1=makeQuery(id+"F5.imprint","IMPRINT",FACE,{"disambiguationData":[TD([[makeQuery(id+"F5.imprint","IMPRINT",EDGE,{"disambiguationData":[TD([[subQ5,1.0]])],"derivedFrom":subQ1}),-1.0]])]});}
            var Q2;
            Q2=sQuery(id+"F4.wireOp",EDGE,"E309.0");
            var Q3;
            Q3=sQuery(id+"F4.wireOp",EDGE,"E307.0");
            var Q4;
            Q4=sQuery(id+"F4.wireOp",EDGE,"E310");
            sweep(context, id + "F6", {"operationType" : NewBodyOperationType.REMOVE, "profiles" : qUnion([Q0, Q1]), "path" : qUnion([Q2, Q3, Q4])});
        }
    });
